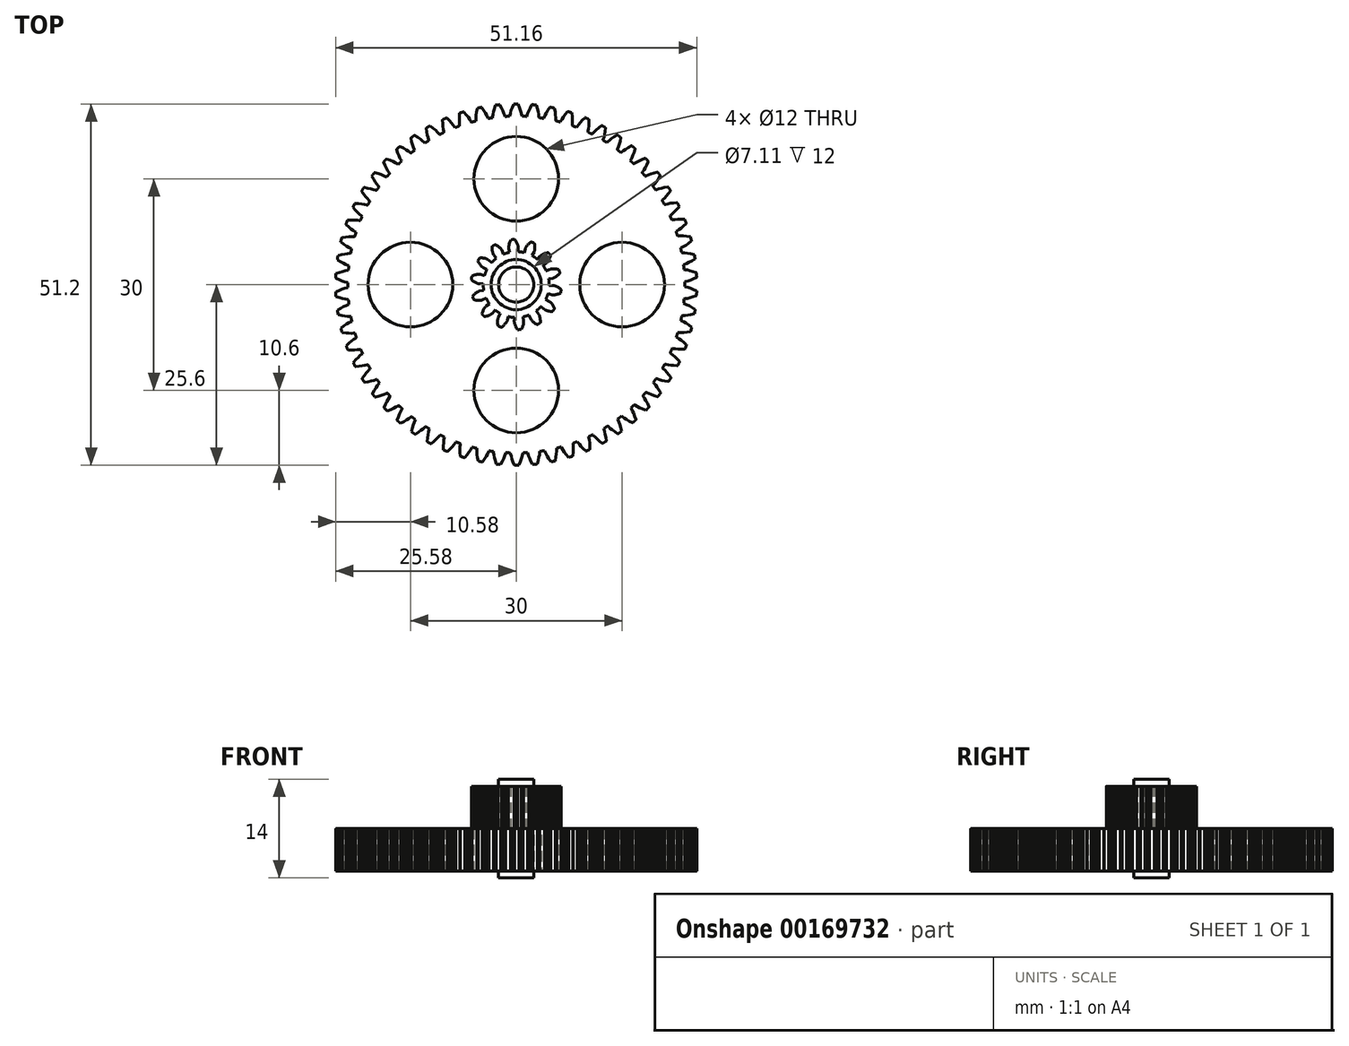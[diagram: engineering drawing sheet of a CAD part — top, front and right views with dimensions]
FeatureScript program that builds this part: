
annotation { "Feature Type Name" : "Feature", "Feature Type Description" : "" }
export const myFeature = defineFeature(function(context is Context, id is Id, definition is map)
    precondition{}
    {
        {
            var Q0;
            Q0=qCreatedBy(makeId("Top.planeOp"),FACE);
            var sketch = newSketch(context, id + "F0", { "sketchPlane" : qUnion([Q0])});
            skLineSegment(sketch, "E0", {"start": v(3, 3.59) * mm, "end": v(3.37, 4.04) * mm});
            skLineSegment(sketch, "E1", {"start": v(3.37, 4.04) * mm, "end": v(3.38, 4.04) * mm});
            skLineSegment(sketch, "E2", {"start": v(3.38, 4.04) * mm, "end": v(3.4, 4.06) * mm});
            skLineSegment(sketch, "E3", {"start": v(3.4, 4.06) * mm, "end": v(3.41, 4.08) * mm});
            skLineSegment(sketch, "E4", {"start": v(3.41, 4.08) * mm, "end": v(3.45, 4.11) * mm});
            skLineSegment(sketch, "E5", {"start": v(3.45, 4.11) * mm, "end": v(3.5, 4.15) * mm});
            skLineSegment(sketch, "E6", {"start": v(3.5, 4.15) * mm, "end": v(3.56, 4.19) * mm});
            skLineSegment(sketch, "E7", {"start": v(3.56, 4.19) * mm, "end": v(3.63, 4.23) * mm});
            skLineSegment(sketch, "E8", {"start": v(3.63, 4.23) * mm, "end": v(3.72, 4.28) * mm});
            skLineSegment(sketch, "E9", {"start": v(3.72, 4.28) * mm, "end": v(3.82, 4.33) * mm});
            skLineSegment(sketch, "E10", {"start": v(3.82, 4.33) * mm, "end": v(3.93, 4.38) * mm});
            skLineSegment(sketch, "E11", {"start": v(3.93, 4.38) * mm, "end": v(4.06, 4.42) * mm});
            skLineSegment(sketch, "E12", {"start": v(4.06, 4.42) * mm, "end": v(4.2, 4.47) * mm});
            skLineSegment(sketch, "E13", {"start": v(4.2, 4.47) * mm, "end": v(4.37, 4.5) * mm});
            skLineSegment(sketch, "E14", {"start": v(4.37, 4.5) * mm, "end": v(4.51, 4.54) * mm});
            skArc(sketch, "E15", {"start": v(4.51, 4.54) * mm, "mid": v(4.7, 4.35) * mm, "end": v(4.86, 4.16) * mm});
            skLineSegment(sketch, "E16", {"start": v(4.86, 4.16) * mm, "end": v(4.82, 4.02) * mm});
            skLineSegment(sketch, "E17", {"start": v(4.82, 4.02) * mm, "end": v(4.77, 3.86) * mm});
            skLineSegment(sketch, "E18", {"start": v(4.77, 3.86) * mm, "end": v(4.72, 3.72) * mm});
            skLineSegment(sketch, "E19", {"start": v(4.72, 3.72) * mm, "end": v(4.66, 3.6) * mm});
            skLineSegment(sketch, "E20", {"start": v(4.66, 3.6) * mm, "end": v(4.6, 3.48) * mm});
            skLineSegment(sketch, "E21", {"start": v(4.6, 3.48) * mm, "end": v(4.55, 3.39) * mm});
            skLineSegment(sketch, "E22", {"start": v(4.55, 3.39) * mm, "end": v(4.5, 3.3) * mm});
            skLineSegment(sketch, "E23", {"start": v(4.5, 3.3) * mm, "end": v(4.44, 3.23) * mm});
            skLineSegment(sketch, "E24", {"start": v(4.44, 3.23) * mm, "end": v(4.4, 3.18) * mm});
            skLineSegment(sketch, "E25", {"start": v(4.4, 3.18) * mm, "end": v(4.36, 3.13) * mm});
            skLineSegment(sketch, "E26", {"start": v(4.36, 3.13) * mm, "end": v(4.32, 3.1) * mm});
            skLineSegment(sketch, "E27", {"start": v(4.32, 3.1) * mm, "end": v(4.3, 3.08) * mm});
            skLineSegment(sketch, "E28", {"start": v(4.3, 3.08) * mm, "end": v(4.29, 3.06) * mm});
            skLineSegment(sketch, "E29", {"start": v(4.29, 3.06) * mm, "end": v(4.28, 3.06) * mm});
            skLineSegment(sketch, "E30", {"start": v(4.28, 3.06) * mm, "end": v(3.8, 2.72) * mm});
            skArc(sketch, "E31", {"start": v(3.8, 2.72) * mm, "mid": v(4.05, 2.34) * mm, "end": v(4.26, 1.93) * mm});
            skLineSegment(sketch, "E32", {"start": v(4.26, 1.93) * mm, "end": v(4.8, 2.18) * mm});
            skLineSegment(sketch, "E33", {"start": v(4.8, 2.18) * mm, "end": v(4.8, 2.18) * mm});
            skLineSegment(sketch, "E34", {"start": v(4.8, 2.18) * mm, "end": v(4.82, 2.19) * mm});
            skLineSegment(sketch, "E35", {"start": v(4.82, 2.19) * mm, "end": v(4.85, 2.2) * mm});
            skLineSegment(sketch, "E36", {"start": v(4.85, 2.2) * mm, "end": v(4.9, 2.2) * mm});
            skLineSegment(sketch, "E37", {"start": v(4.9, 2.2) * mm, "end": v(4.95, 2.22) * mm});
            skLineSegment(sketch, "E38", {"start": v(4.95, 2.22) * mm, "end": v(5.02, 2.23) * mm});
            skLineSegment(sketch, "E39", {"start": v(5.02, 2.23) * mm, "end": v(5.1, 2.24) * mm});
            skLineSegment(sketch, "E40", {"start": v(5.1, 2.24) * mm, "end": v(5.2, 2.24) * mm});
            skLineSegment(sketch, "E41", {"start": v(5.2, 2.24) * mm, "end": v(5.32, 2.24) * mm});
            skLineSegment(sketch, "E42", {"start": v(5.32, 2.24) * mm, "end": v(5.44, 2.24) * mm});
            skLineSegment(sketch, "E43", {"start": v(5.44, 2.24) * mm, "end": v(5.58, 2.22) * mm});
            skLineSegment(sketch, "E44", {"start": v(5.58, 2.22) * mm, "end": v(5.73, 2.2) * mm});
            skLineSegment(sketch, "E45", {"start": v(5.73, 2.2) * mm, "end": v(5.89, 2.17) * mm});
            skLineSegment(sketch, "E46", {"start": v(5.89, 2.17) * mm, "end": v(6.03, 2.13) * mm});
            skArc(sketch, "E47", {"start": v(6.03, 2.13) * mm, "mid": v(6.12, 1.89) * mm, "end": v(6.19, 1.64) * mm});
            skLineSegment(sketch, "E48", {"start": v(6.19, 1.64) * mm, "end": v(6.09, 1.53) * mm});
            skLineSegment(sketch, "E49", {"start": v(6.09, 1.53) * mm, "end": v(5.97, 1.4) * mm});
            skLineSegment(sketch, "E50", {"start": v(5.97, 1.4) * mm, "end": v(5.86, 1.3) * mm});
            skLineSegment(sketch, "E51", {"start": v(5.86, 1.3) * mm, "end": v(5.76, 1.22) * mm});
            skLineSegment(sketch, "E52", {"start": v(5.76, 1.22) * mm, "end": v(5.66, 1.14) * mm});
            skLineSegment(sketch, "E53", {"start": v(5.66, 1.14) * mm, "end": v(5.56, 1.08) * mm});
            skLineSegment(sketch, "E54", {"start": v(5.56, 1.08) * mm, "end": v(5.48, 1.03) * mm});
            skLineSegment(sketch, "E55", {"start": v(5.48, 1.03) * mm, "end": v(5.4, 0.99) * mm});
            skLineSegment(sketch, "E56", {"start": v(5.4, 0.99) * mm, "end": v(5.34, 0.96) * mm});
            skLineSegment(sketch, "E57", {"start": v(5.34, 0.96) * mm, "end": v(5.28, 0.93) * mm});
            skLineSegment(sketch, "E58", {"start": v(5.28, 0.93) * mm, "end": v(5.24, 0.92) * mm});
            skLineSegment(sketch, "E59", {"start": v(5.24, 0.92) * mm, "end": v(5.21, 0.9) * mm});
            skLineSegment(sketch, "E60", {"start": v(5.21, 0.9) * mm, "end": v(5.2, 0.9) * mm});
            skLineSegment(sketch, "E61", {"start": v(5.2, 0.9) * mm, "end": v(5.18, 0.9) * mm});
            skLineSegment(sketch, "E62", {"start": v(5.18, 0.9) * mm, "end": v(4.6, 0.8) * mm});
            skArc(sketch, "E63", {"start": v(4.6, 0.8) * mm, "mid": v(4.66, 0.35) * mm, "end": v(4.67, -0.1) * mm});
            skLineSegment(sketch, "E64", {"start": v(4.67, -0.1) * mm, "end": v(5.26, -0.12) * mm});
            skLineSegment(sketch, "E65", {"start": v(5.26, -0.12) * mm, "end": v(5.27, -0.12) * mm});
            skLineSegment(sketch, "E66", {"start": v(5.27, -0.12) * mm, "end": v(5.29, -0.12) * mm});
            skLineSegment(sketch, "E67", {"start": v(5.29, -0.12) * mm, "end": v(5.32, -0.13) * mm});
            skLineSegment(sketch, "E68", {"start": v(5.32, -0.13) * mm, "end": v(5.36, -0.13) * mm});
            skLineSegment(sketch, "E69", {"start": v(5.36, -0.13) * mm, "end": v(5.42, -0.15) * mm});
            skLineSegment(sketch, "E70", {"start": v(5.42, -0.15) * mm, "end": v(5.5, -0.17) * mm});
            skLineSegment(sketch, "E71", {"start": v(5.5, -0.17) * mm, "end": v(5.57, -0.2) * mm});
            skLineSegment(sketch, "E72", {"start": v(5.57, -0.2) * mm, "end": v(5.66, -0.24) * mm});
            skLineSegment(sketch, "E73", {"start": v(5.66, -0.24) * mm, "end": v(5.76, -0.29) * mm});
            skLineSegment(sketch, "E74", {"start": v(5.76, -0.29) * mm, "end": v(5.87, -0.35) * mm});
            skLineSegment(sketch, "E75", {"start": v(5.87, -0.35) * mm, "end": v(6, -0.42) * mm});
            skLineSegment(sketch, "E76", {"start": v(6, -0.42) * mm, "end": v(6.12, -0.5) * mm});
            skLineSegment(sketch, "E77", {"start": v(6.12, -0.5) * mm, "end": v(6.25, -0.6) * mm});
            skLineSegment(sketch, "E78", {"start": v(6.25, -0.6) * mm, "end": v(6.36, -0.7) * mm});
            skArc(sketch, "E79", {"start": v(6.36, -0.7) * mm, "mid": v(6.33, -0.95) * mm, "end": v(6.28, -1.2) * mm});
            skLineSegment(sketch, "E80", {"start": v(6.28, -1.2) * mm, "end": v(6.15, -1.27) * mm});
            skLineSegment(sketch, "E81", {"start": v(6.15, -1.27) * mm, "end": v(6, -1.32) * mm});
            skLineSegment(sketch, "E82", {"start": v(6, -1.32) * mm, "end": v(5.85, -1.37) * mm});
            skLineSegment(sketch, "E83", {"start": v(5.85, -1.37) * mm, "end": v(5.71, -1.4) * mm});
            skLineSegment(sketch, "E84", {"start": v(5.71, -1.4) * mm, "end": v(5.6, -1.43) * mm});
            skLineSegment(sketch, "E85", {"start": v(5.6, -1.43) * mm, "end": v(5.48, -1.44) * mm});
            skLineSegment(sketch, "E86", {"start": v(5.48, -1.44) * mm, "end": v(5.38, -1.45) * mm});
            skLineSegment(sketch, "E87", {"start": v(5.38, -1.45) * mm, "end": v(5.3, -1.46) * mm});
            skLineSegment(sketch, "E88", {"start": v(5.3, -1.46) * mm, "end": v(5.23, -1.46) * mm});
            skLineSegment(sketch, "E89", {"start": v(5.23, -1.46) * mm, "end": v(5.17, -1.45) * mm});
            skLineSegment(sketch, "E90", {"start": v(5.17, -1.45) * mm, "end": v(5.12, -1.45) * mm});
            skLineSegment(sketch, "E91", {"start": v(5.12, -1.45) * mm, "end": v(5.09, -1.44) * mm});
            skLineSegment(sketch, "E92", {"start": v(5.09, -1.44) * mm, "end": v(5.07, -1.44) * mm});
            skLineSegment(sketch, "E93", {"start": v(5.07, -1.44) * mm, "end": v(5.06, -1.44) * mm});
            skLineSegment(sketch, "E94", {"start": v(5.06, -1.44) * mm, "end": v(4.5, -1.28) * mm});
            skArc(sketch, "E95", {"start": v(4.5, -1.28) * mm, "mid": v(4.35, -1.7) * mm, "end": v(4.16, -2.12) * mm});
            skLineSegment(sketch, "E96", {"start": v(4.16, -2.12) * mm, "end": v(4.69, -2.39) * mm});
            skLineSegment(sketch, "E97", {"start": v(4.69, -2.39) * mm, "end": v(4.7, -2.4) * mm});
            skLineSegment(sketch, "E98", {"start": v(4.7, -2.4) * mm, "end": v(4.71, -2.4) * mm});
            skLineSegment(sketch, "E99", {"start": v(4.71, -2.4) * mm, "end": v(4.74, -2.42) * mm});
            skLineSegment(sketch, "E100", {"start": v(4.74, -2.42) * mm, "end": v(4.78, -2.45) * mm});
            skLineSegment(sketch, "E101", {"start": v(4.78, -2.45) * mm, "end": v(4.82, -2.49) * mm});
            skLineSegment(sketch, "E102", {"start": v(4.82, -2.49) * mm, "end": v(4.87, -2.54) * mm});
            skLineSegment(sketch, "E103", {"start": v(4.87, -2.54) * mm, "end": v(4.93, -2.6) * mm});
            skLineSegment(sketch, "E104", {"start": v(4.93, -2.6) * mm, "end": v(5, -2.67) * mm});
            skLineSegment(sketch, "E105", {"start": v(5, -2.67) * mm, "end": v(5.07, -2.76) * mm});
            skLineSegment(sketch, "E106", {"start": v(5.07, -2.76) * mm, "end": v(5.14, -2.86) * mm});
            skLineSegment(sketch, "E107", {"start": v(5.14, -2.86) * mm, "end": v(5.22, -2.98) * mm});
            skLineSegment(sketch, "E108", {"start": v(5.22, -2.98) * mm, "end": v(5.3, -3.1) * mm});
            skLineSegment(sketch, "E109", {"start": v(5.3, -3.1) * mm, "end": v(5.37, -3.25) * mm});
            skLineSegment(sketch, "E110", {"start": v(5.37, -3.25) * mm, "end": v(5.43, -3.39) * mm});
            skArc(sketch, "E111", {"start": v(5.43, -3.39) * mm, "mid": v(5.29, -3.6) * mm, "end": v(5.14, -3.82) * mm});
            skLineSegment(sketch, "E112", {"start": v(5.14, -3.82) * mm, "end": v(4.99, -3.8) * mm});
            skLineSegment(sketch, "E113", {"start": v(4.99, -3.8) * mm, "end": v(4.83, -3.8) * mm});
            skLineSegment(sketch, "E114", {"start": v(4.83, -3.8) * mm, "end": v(4.68, -3.77) * mm});
            skLineSegment(sketch, "E115", {"start": v(4.68, -3.77) * mm, "end": v(4.54, -3.74) * mm});
            skLineSegment(sketch, "E116", {"start": v(4.54, -3.74) * mm, "end": v(4.42, -3.71) * mm});
            skLineSegment(sketch, "E117", {"start": v(4.42, -3.71) * mm, "end": v(4.31, -3.68) * mm});
            skLineSegment(sketch, "E118", {"start": v(4.31, -3.68) * mm, "end": v(4.22, -3.64) * mm});
            skLineSegment(sketch, "E119", {"start": v(4.22, -3.64) * mm, "end": v(4.14, -3.61) * mm});
            skLineSegment(sketch, "E120", {"start": v(4.14, -3.61) * mm, "end": v(4.08, -3.58) * mm});
            skLineSegment(sketch, "E121", {"start": v(4.08, -3.58) * mm, "end": v(4.02, -3.55) * mm});
            skLineSegment(sketch, "E122", {"start": v(4.02, -3.55) * mm, "end": v(3.98, -3.53) * mm});
            skLineSegment(sketch, "E123", {"start": v(3.98, -3.53) * mm, "end": v(3.96, -3.5) * mm});
            skLineSegment(sketch, "E124", {"start": v(3.96, -3.5) * mm, "end": v(3.94, -3.5) * mm});
            skLineSegment(sketch, "E125", {"start": v(3.94, -3.5) * mm, "end": v(3.94, -3.5) * mm});
            skLineSegment(sketch, "E126", {"start": v(3.94, -3.5) * mm, "end": v(3.5, -3.1) * mm});
            skArc(sketch, "E127", {"start": v(3.5, -3.1) * mm, "mid": v(3.18, -3.43) * mm, "end": v(2.83, -3.72) * mm});
            skLineSegment(sketch, "E128", {"start": v(2.83, -3.72) * mm, "end": v(3.19, -4.19) * mm});
            skLineSegment(sketch, "E129", {"start": v(3.19, -4.19) * mm, "end": v(3.2, -4.2) * mm});
            skLineSegment(sketch, "E130", {"start": v(3.2, -4.2) * mm, "end": v(3.2, -4.2) * mm});
            skLineSegment(sketch, "E131", {"start": v(3.2, -4.2) * mm, "end": v(3.22, -4.24) * mm});
            skLineSegment(sketch, "E132", {"start": v(3.22, -4.24) * mm, "end": v(3.24, -4.28) * mm});
            skLineSegment(sketch, "E133", {"start": v(3.24, -4.28) * mm, "end": v(3.26, -4.33) * mm});
            skLineSegment(sketch, "E134", {"start": v(3.26, -4.33) * mm, "end": v(3.3, -4.4) * mm});
            skLineSegment(sketch, "E135", {"start": v(3.3, -4.4) * mm, "end": v(3.32, -4.48) * mm});
            skLineSegment(sketch, "E136", {"start": v(3.32, -4.48) * mm, "end": v(3.35, -4.58) * mm});
            skLineSegment(sketch, "E137", {"start": v(3.35, -4.58) * mm, "end": v(3.37, -4.68) * mm});
            skLineSegment(sketch, "E138", {"start": v(3.37, -4.68) * mm, "end": v(3.4, -4.8) * mm});
            skLineSegment(sketch, "E139", {"start": v(3.4, -4.8) * mm, "end": v(3.4, -4.94) * mm});
            skLineSegment(sketch, "E140", {"start": v(3.4, -4.94) * mm, "end": v(3.42, -5.1) * mm});
            skLineSegment(sketch, "E141", {"start": v(3.42, -5.1) * mm, "end": v(3.42, -5.26) * mm});
            skLineSegment(sketch, "E142", {"start": v(3.42, -5.26) * mm, "end": v(3.42, -5.4) * mm});
            skArc(sketch, "E143", {"start": v(3.42, -5.4) * mm, "mid": v(3.2, -5.54) * mm, "end": v(2.97, -5.67) * mm});
            skLineSegment(sketch, "E144", {"start": v(2.97, -5.67) * mm, "end": v(2.84, -5.6) * mm});
            skLineSegment(sketch, "E145", {"start": v(2.84, -5.6) * mm, "end": v(2.7, -5.5) * mm});
            skLineSegment(sketch, "E146", {"start": v(2.7, -5.5) * mm, "end": v(2.58, -5.42) * mm});
            skLineSegment(sketch, "E147", {"start": v(2.58, -5.42) * mm, "end": v(2.47, -5.34) * mm});
            skLineSegment(sketch, "E148", {"start": v(2.47, -5.34) * mm, "end": v(2.37, -5.26) * mm});
            skLineSegment(sketch, "E149", {"start": v(2.37, -5.26) * mm, "end": v(2.29, -5.18) * mm});
            skLineSegment(sketch, "E150", {"start": v(2.29, -5.18) * mm, "end": v(2.22, -5.11) * mm});
            skLineSegment(sketch, "E151", {"start": v(2.22, -5.11) * mm, "end": v(2.16, -5.05) * mm});
            skLineSegment(sketch, "E152", {"start": v(2.16, -5.05) * mm, "end": v(2.12, -5) * mm});
            skLineSegment(sketch, "E153", {"start": v(2.12, -5) * mm, "end": v(2.08, -4.94) * mm});
            skLineSegment(sketch, "E154", {"start": v(2.08, -4.94) * mm, "end": v(2.06, -4.9) * mm});
            skLineSegment(sketch, "E155", {"start": v(2.06, -4.9) * mm, "end": v(2.04, -4.88) * mm});
            skLineSegment(sketch, "E156", {"start": v(2.04, -4.88) * mm, "end": v(2.03, -4.86) * mm});
            skLineSegment(sketch, "E157", {"start": v(2.03, -4.86) * mm, "end": v(2.03, -4.85) * mm});
            skLineSegment(sketch, "E158", {"start": v(2.03, -4.85) * mm, "end": v(1.8, -4.31) * mm});
            skArc(sketch, "E159", {"start": v(1.8, -4.31) * mm, "mid": v(1.38, -4.47) * mm, "end": v(0.94, -4.58) * mm});
            skLineSegment(sketch, "E160", {"start": v(0.94, -4.58) * mm, "end": v(1.06, -5.16) * mm});
            skLineSegment(sketch, "E161", {"start": v(1.06, -5.16) * mm, "end": v(1.06, -5.16) * mm});
            skLineSegment(sketch, "E162", {"start": v(1.06, -5.16) * mm, "end": v(1.06, -5.18) * mm});
            skLineSegment(sketch, "E163", {"start": v(1.06, -5.18) * mm, "end": v(1.06, -5.21) * mm});
            skLineSegment(sketch, "E164", {"start": v(1.06, -5.21) * mm, "end": v(1.06, -5.26) * mm});
            skLineSegment(sketch, "E165", {"start": v(1.06, -5.26) * mm, "end": v(1.06, -5.32) * mm});
            skLineSegment(sketch, "E166", {"start": v(1.06, -5.32) * mm, "end": v(1.06, -5.4) * mm});
            skLineSegment(sketch, "E167", {"start": v(1.06, -5.4) * mm, "end": v(1.05, -5.48) * mm});
            skLineSegment(sketch, "E168", {"start": v(1.05, -5.48) * mm, "end": v(1.03, -5.57) * mm});
            skLineSegment(sketch, "E169", {"start": v(1.03, -5.57) * mm, "end": v(1, -5.68) * mm});
            skLineSegment(sketch, "E170", {"start": v(1, -5.68) * mm, "end": v(0.97, -5.8) * mm});
            skLineSegment(sketch, "E171", {"start": v(0.97, -5.8) * mm, "end": v(0.93, -5.93) * mm});
            skLineSegment(sketch, "E172", {"start": v(0.93, -5.93) * mm, "end": v(0.87, -6.07) * mm});
            skLineSegment(sketch, "E173", {"start": v(0.87, -6.07) * mm, "end": v(0.8, -6.22) * mm});
            skLineSegment(sketch, "E174", {"start": v(0.8, -6.22) * mm, "end": v(0.74, -6.36) * mm});
            skArc(sketch, "E175", {"start": v(0.74, -6.36) * mm, "mid": v(0.48, -6.38) * mm, "end": v(0.22, -6.4) * mm});
            skLineSegment(sketch, "E176", {"start": v(0.22, -6.4) * mm, "end": v(0.13, -6.27) * mm});
            skLineSegment(sketch, "E177", {"start": v(0.13, -6.27) * mm, "end": v(0.04, -6.14) * mm});
            skLineSegment(sketch, "E178", {"start": v(0.04, -6.14) * mm, "end": v(-0.03, -6) * mm});
            skLineSegment(sketch, "E179", {"start": v(-0.03, -6) * mm, "end": v(-0.1, -5.88) * mm});
            skLineSegment(sketch, "E180", {"start": v(-0.1, -5.88) * mm, "end": v(-0.15, -5.77) * mm});
            skLineSegment(sketch, "E181", {"start": v(-0.15, -5.77) * mm, "end": v(-0.19, -5.66) * mm});
            skLineSegment(sketch, "E182", {"start": v(-0.19, -5.66) * mm, "end": v(-0.22, -5.57) * mm});
            skLineSegment(sketch, "E183", {"start": v(-0.22, -5.57) * mm, "end": v(-0.24, -5.49) * mm});
            skLineSegment(sketch, "E184", {"start": v(-0.24, -5.49) * mm, "end": v(-0.26, -5.42) * mm});
            skLineSegment(sketch, "E185", {"start": v(-0.26, -5.42) * mm, "end": v(-0.27, -5.36) * mm});
            skLineSegment(sketch, "E186", {"start": v(-0.27, -5.36) * mm, "end": v(-0.27, -5.31) * mm});
            skLineSegment(sketch, "E187", {"start": v(-0.27, -5.31) * mm, "end": v(-0.28, -5.28) * mm});
            skLineSegment(sketch, "E188", {"start": v(-0.28, -5.28) * mm, "end": v(-0.28, -5.26) * mm});
            skLineSegment(sketch, "E189", {"start": v(-0.28, -5.26) * mm, "end": v(-0.28, -5.26) * mm});
            skLineSegment(sketch, "E190", {"start": v(-0.28, -5.26) * mm, "end": v(-0.24, -4.67) * mm});
            skArc(sketch, "E191", {"start": v(-0.24, -4.67) * mm, "mid": v(-0.7, -4.62) * mm, "end": v(-1.14, -4.53) * mm});
            skLineSegment(sketch, "E192", {"start": v(-1.14, -4.53) * mm, "end": v(-1.29, -5.1) * mm});
            skLineSegment(sketch, "E193", {"start": v(-1.29, -5.1) * mm, "end": v(-1.29, -5.1) * mm});
            skLineSegment(sketch, "E194", {"start": v(-1.29, -5.1) * mm, "end": v(-1.3, -5.13) * mm});
            skLineSegment(sketch, "E195", {"start": v(-1.3, -5.13) * mm, "end": v(-1.3, -5.16) * mm});
            skLineSegment(sketch, "E196", {"start": v(-1.3, -5.16) * mm, "end": v(-1.32, -5.2) * mm});
            skLineSegment(sketch, "E197", {"start": v(-1.32, -5.2) * mm, "end": v(-1.35, -5.25) * mm});
            skLineSegment(sketch, "E198", {"start": v(-1.35, -5.25) * mm, "end": v(-1.39, -5.32) * mm});
            skLineSegment(sketch, "E199", {"start": v(-1.39, -5.32) * mm, "end": v(-1.43, -5.39) * mm});
            skLineSegment(sketch, "E200", {"start": v(-1.43, -5.39) * mm, "end": v(-1.5, -5.47) * mm});
            skLineSegment(sketch, "E201", {"start": v(-1.5, -5.47) * mm, "end": v(-1.56, -5.56) * mm});
            skLineSegment(sketch, "E202", {"start": v(-1.56, -5.56) * mm, "end": v(-1.64, -5.65) * mm});
            skLineSegment(sketch, "E203", {"start": v(-1.64, -5.65) * mm, "end": v(-1.74, -5.75) * mm});
            skLineSegment(sketch, "E204", {"start": v(-1.74, -5.75) * mm, "end": v(-1.85, -5.85) * mm});
            skLineSegment(sketch, "E205", {"start": v(-1.85, -5.85) * mm, "end": v(-1.98, -5.96) * mm});
            skLineSegment(sketch, "E206", {"start": v(-1.98, -5.96) * mm, "end": v(-2.1, -6.05) * mm});
            skArc(sketch, "E207", {"start": v(-2.1, -6.05) * mm, "mid": v(-2.34, -5.96) * mm, "end": v(-2.58, -5.86) * mm});
            skLineSegment(sketch, "E208", {"start": v(-2.58, -5.86) * mm, "end": v(-2.6, -5.71) * mm});
            skLineSegment(sketch, "E209", {"start": v(-2.6, -5.71) * mm, "end": v(-2.62, -5.55) * mm});
            skLineSegment(sketch, "E210", {"start": v(-2.62, -5.55) * mm, "end": v(-2.63, -5.4) * mm});
            skLineSegment(sketch, "E211", {"start": v(-2.63, -5.4) * mm, "end": v(-2.64, -5.26) * mm});
            skLineSegment(sketch, "E212", {"start": v(-2.64, -5.26) * mm, "end": v(-2.63, -5.13) * mm});
            skLineSegment(sketch, "E213", {"start": v(-2.63, -5.13) * mm, "end": v(-2.63, -5.02) * mm});
            skLineSegment(sketch, "E214", {"start": v(-2.63, -5.02) * mm, "end": v(-2.61, -4.92) * mm});
            skLineSegment(sketch, "E215", {"start": v(-2.61, -4.92) * mm, "end": v(-2.6, -4.84) * mm});
            skLineSegment(sketch, "E216", {"start": v(-2.6, -4.84) * mm, "end": v(-2.58, -4.77) * mm});
            skLineSegment(sketch, "E217", {"start": v(-2.58, -4.77) * mm, "end": v(-2.57, -4.71) * mm});
            skLineSegment(sketch, "E218", {"start": v(-2.57, -4.71) * mm, "end": v(-2.55, -4.67) * mm});
            skLineSegment(sketch, "E219", {"start": v(-2.55, -4.67) * mm, "end": v(-2.54, -4.64) * mm});
            skLineSegment(sketch, "E220", {"start": v(-2.54, -4.64) * mm, "end": v(-2.53, -4.62) * mm});
            skLineSegment(sketch, "E221", {"start": v(-2.53, -4.62) * mm, "end": v(-2.53, -4.62) * mm});
            skLineSegment(sketch, "E222", {"start": v(-2.53, -4.62) * mm, "end": v(-2.25, -4.1) * mm});
            skArc(sketch, "E223", {"start": v(-2.25, -4.1) * mm, "mid": v(-2.63, -3.86) * mm, "end": v(-3, -3.59) * mm});
            skLineSegment(sketch, "E224", {"start": v(-3, -3.59) * mm, "end": v(-3.37, -4.04) * mm});
            skLineSegment(sketch, "E225", {"start": v(-3.37, -4.04) * mm, "end": v(-3.38, -4.04) * mm});
            skLineSegment(sketch, "E226", {"start": v(-3.38, -4.04) * mm, "end": v(-3.4, -4.06) * mm});
            skLineSegment(sketch, "E227", {"start": v(-3.4, -4.06) * mm, "end": v(-3.41, -4.08) * mm});
            skLineSegment(sketch, "E228", {"start": v(-3.41, -4.08) * mm, "end": v(-3.45, -4.11) * mm});
            skLineSegment(sketch, "E229", {"start": v(-3.45, -4.11) * mm, "end": v(-3.5, -4.15) * mm});
            skLineSegment(sketch, "E230", {"start": v(-3.5, -4.15) * mm, "end": v(-3.56, -4.19) * mm});
            skLineSegment(sketch, "E231", {"start": v(-3.56, -4.19) * mm, "end": v(-3.63, -4.23) * mm});
            skLineSegment(sketch, "E232", {"start": v(-3.63, -4.23) * mm, "end": v(-3.72, -4.28) * mm});
            skLineSegment(sketch, "E233", {"start": v(-3.72, -4.28) * mm, "end": v(-3.82, -4.33) * mm});
            skLineSegment(sketch, "E234", {"start": v(-3.82, -4.33) * mm, "end": v(-3.93, -4.38) * mm});
            skLineSegment(sketch, "E235", {"start": v(-3.93, -4.38) * mm, "end": v(-4.06, -4.42) * mm});
            skLineSegment(sketch, "E236", {"start": v(-4.06, -4.42) * mm, "end": v(-4.2, -4.47) * mm});
            skLineSegment(sketch, "E237", {"start": v(-4.2, -4.47) * mm, "end": v(-4.37, -4.5) * mm});
            skLineSegment(sketch, "E238", {"start": v(-4.37, -4.5) * mm, "end": v(-4.51, -4.54) * mm});
            skArc(sketch, "E239", {"start": v(-4.51, -4.54) * mm, "mid": v(-4.7, -4.35) * mm, "end": v(-4.86, -4.16) * mm});
            skLineSegment(sketch, "E240", {"start": v(-4.86, -4.16) * mm, "end": v(-4.82, -4.02) * mm});
            skLineSegment(sketch, "E241", {"start": v(-4.82, -4.02) * mm, "end": v(-4.77, -3.86) * mm});
            skLineSegment(sketch, "E242", {"start": v(-4.77, -3.86) * mm, "end": v(-4.72, -3.72) * mm});
            skLineSegment(sketch, "E243", {"start": v(-4.72, -3.72) * mm, "end": v(-4.66, -3.6) * mm});
            skLineSegment(sketch, "E244", {"start": v(-4.66, -3.6) * mm, "end": v(-4.6, -3.48) * mm});
            skLineSegment(sketch, "E245", {"start": v(-4.6, -3.48) * mm, "end": v(-4.55, -3.39) * mm});
            skLineSegment(sketch, "E246", {"start": v(-4.55, -3.39) * mm, "end": v(-4.5, -3.3) * mm});
            skLineSegment(sketch, "E247", {"start": v(-4.5, -3.3) * mm, "end": v(-4.44, -3.23) * mm});
            skLineSegment(sketch, "E248", {"start": v(-4.44, -3.23) * mm, "end": v(-4.4, -3.18) * mm});
            skLineSegment(sketch, "E249", {"start": v(-4.4, -3.18) * mm, "end": v(-4.36, -3.13) * mm});
            skLineSegment(sketch, "E250", {"start": v(-4.36, -3.13) * mm, "end": v(-4.32, -3.1) * mm});
            skLineSegment(sketch, "E251", {"start": v(-4.32, -3.1) * mm, "end": v(-4.3, -3.08) * mm});
            skLineSegment(sketch, "E252", {"start": v(-4.3, -3.08) * mm, "end": v(-4.29, -3.06) * mm});
            skLineSegment(sketch, "E253", {"start": v(-4.29, -3.06) * mm, "end": v(-4.28, -3.06) * mm});
            skLineSegment(sketch, "E254", {"start": v(-4.28, -3.06) * mm, "end": v(-3.8, -2.72) * mm});
            skArc(sketch, "E255", {"start": v(-3.8, -2.72) * mm, "mid": v(-4.05, -2.34) * mm, "end": v(-4.26, -1.93) * mm});
            skLineSegment(sketch, "E256", {"start": v(-4.26, -1.93) * mm, "end": v(-4.8, -2.18) * mm});
            skLineSegment(sketch, "E257", {"start": v(-4.8, -2.18) * mm, "end": v(-4.8, -2.18) * mm});
            skLineSegment(sketch, "E258", {"start": v(-4.8, -2.18) * mm, "end": v(-4.82, -2.19) * mm});
            skLineSegment(sketch, "E259", {"start": v(-4.82, -2.19) * mm, "end": v(-4.85, -2.2) * mm});
            skLineSegment(sketch, "E260", {"start": v(-4.85, -2.2) * mm, "end": v(-4.9, -2.2) * mm});
            skLineSegment(sketch, "E261", {"start": v(-4.9, -2.2) * mm, "end": v(-4.95, -2.22) * mm});
            skLineSegment(sketch, "E262", {"start": v(-4.95, -2.22) * mm, "end": v(-5.02, -2.23) * mm});
            skLineSegment(sketch, "E263", {"start": v(-5.02, -2.23) * mm, "end": v(-5.1, -2.24) * mm});
            skLineSegment(sketch, "E264", {"start": v(-5.1, -2.24) * mm, "end": v(-5.2, -2.24) * mm});
            skLineSegment(sketch, "E265", {"start": v(-5.2, -2.24) * mm, "end": v(-5.32, -2.24) * mm});
            skLineSegment(sketch, "E266", {"start": v(-5.32, -2.24) * mm, "end": v(-5.44, -2.24) * mm});
            skLineSegment(sketch, "E267", {"start": v(-5.44, -2.24) * mm, "end": v(-5.58, -2.22) * mm});
            skLineSegment(sketch, "E268", {"start": v(-5.58, -2.22) * mm, "end": v(-5.73, -2.2) * mm});
            skLineSegment(sketch, "E269", {"start": v(-5.73, -2.2) * mm, "end": v(-5.89, -2.17) * mm});
            skLineSegment(sketch, "E270", {"start": v(-5.89, -2.17) * mm, "end": v(-6.03, -2.13) * mm});
            skArc(sketch, "E271", {"start": v(-6.03, -2.13) * mm, "mid": v(-6.12, -1.89) * mm, "end": v(-6.19, -1.64) * mm});
            skLineSegment(sketch, "E272", {"start": v(-6.19, -1.64) * mm, "end": v(-6.09, -1.53) * mm});
            skLineSegment(sketch, "E273", {"start": v(-6.09, -1.53) * mm, "end": v(-5.97, -1.4) * mm});
            skLineSegment(sketch, "E274", {"start": v(-5.97, -1.4) * mm, "end": v(-5.86, -1.3) * mm});
            skLineSegment(sketch, "E275", {"start": v(-5.86, -1.3) * mm, "end": v(-5.76, -1.22) * mm});
            skLineSegment(sketch, "E276", {"start": v(-5.76, -1.22) * mm, "end": v(-5.66, -1.14) * mm});
            skLineSegment(sketch, "E277", {"start": v(-5.66, -1.14) * mm, "end": v(-5.56, -1.08) * mm});
            skLineSegment(sketch, "E278", {"start": v(-5.56, -1.08) * mm, "end": v(-5.48, -1.03) * mm});
            skLineSegment(sketch, "E279", {"start": v(-5.48, -1.03) * mm, "end": v(-5.4, -0.99) * mm});
            skLineSegment(sketch, "E280", {"start": v(-5.4, -0.99) * mm, "end": v(-5.34, -0.96) * mm});
            skLineSegment(sketch, "E281", {"start": v(-5.34, -0.96) * mm, "end": v(-5.28, -0.93) * mm});
            skLineSegment(sketch, "E282", {"start": v(-5.28, -0.93) * mm, "end": v(-5.24, -0.92) * mm});
            skLineSegment(sketch, "E283", {"start": v(-5.24, -0.92) * mm, "end": v(-5.21, -0.9) * mm});
            skLineSegment(sketch, "E284", {"start": v(-5.21, -0.9) * mm, "end": v(-5.2, -0.9) * mm});
            skLineSegment(sketch, "E285", {"start": v(-5.2, -0.9) * mm, "end": v(-5.18, -0.9) * mm});
            skLineSegment(sketch, "E286", {"start": v(-5.18, -0.9) * mm, "end": v(-4.6, -0.8) * mm});
            skArc(sketch, "E287", {"start": v(-4.6, -0.8) * mm, "mid": v(-4.66, -0.35) * mm, "end": v(-4.67, 0.1) * mm});
            skLineSegment(sketch, "E288", {"start": v(-4.67, 0.1) * mm, "end": v(-5.26, 0.12) * mm});
            skLineSegment(sketch, "E289", {"start": v(-5.26, 0.12) * mm, "end": v(-5.27, 0.12) * mm});
            skLineSegment(sketch, "E290", {"start": v(-5.27, 0.12) * mm, "end": v(-5.29, 0.12) * mm});
            skLineSegment(sketch, "E291", {"start": v(-5.29, 0.12) * mm, "end": v(-5.32, 0.13) * mm});
            skLineSegment(sketch, "E292", {"start": v(-5.32, 0.13) * mm, "end": v(-5.36, 0.13) * mm});
            skLineSegment(sketch, "E293", {"start": v(-5.36, 0.13) * mm, "end": v(-5.42, 0.15) * mm});
            skLineSegment(sketch, "E294", {"start": v(-5.42, 0.15) * mm, "end": v(-5.5, 0.17) * mm});
            skLineSegment(sketch, "E295", {"start": v(-5.5, 0.17) * mm, "end": v(-5.57, 0.2) * mm});
            skLineSegment(sketch, "E296", {"start": v(-5.57, 0.2) * mm, "end": v(-5.66, 0.24) * mm});
            skLineSegment(sketch, "E297", {"start": v(-5.66, 0.24) * mm, "end": v(-5.76, 0.29) * mm});
            skLineSegment(sketch, "E298", {"start": v(-5.76, 0.29) * mm, "end": v(-5.87, 0.35) * mm});
            skLineSegment(sketch, "E299", {"start": v(-5.87, 0.35) * mm, "end": v(-6, 0.42) * mm});
            skLineSegment(sketch, "E300", {"start": v(-6, 0.42) * mm, "end": v(-6.12, 0.5) * mm});
            skLineSegment(sketch, "E301", {"start": v(-6.12, 0.5) * mm, "end": v(-6.25, 0.6) * mm});
            skLineSegment(sketch, "E302", {"start": v(-6.25, 0.6) * mm, "end": v(-6.36, 0.7) * mm});
            skArc(sketch, "E303", {"start": v(-6.36, 0.7) * mm, "mid": v(-6.33, 0.95) * mm, "end": v(-6.28, 1.2) * mm});
            skLineSegment(sketch, "E304", {"start": v(-6.28, 1.2) * mm, "end": v(-6.15, 1.27) * mm});
            skLineSegment(sketch, "E305", {"start": v(-6.15, 1.27) * mm, "end": v(-6, 1.32) * mm});
            skLineSegment(sketch, "E306", {"start": v(-6, 1.32) * mm, "end": v(-5.85, 1.37) * mm});
            skLineSegment(sketch, "E307", {"start": v(-5.85, 1.37) * mm, "end": v(-5.71, 1.4) * mm});
            skLineSegment(sketch, "E308", {"start": v(-5.71, 1.4) * mm, "end": v(-5.6, 1.43) * mm});
            skLineSegment(sketch, "E309", {"start": v(-5.6, 1.43) * mm, "end": v(-5.48, 1.44) * mm});
            skLineSegment(sketch, "E310", {"start": v(-5.48, 1.44) * mm, "end": v(-5.38, 1.45) * mm});
            skLineSegment(sketch, "E311", {"start": v(-5.38, 1.45) * mm, "end": v(-5.3, 1.46) * mm});
            skLineSegment(sketch, "E312", {"start": v(-5.3, 1.46) * mm, "end": v(-5.23, 1.46) * mm});
            skLineSegment(sketch, "E313", {"start": v(-5.23, 1.46) * mm, "end": v(-5.17, 1.45) * mm});
            skLineSegment(sketch, "E314", {"start": v(-5.17, 1.45) * mm, "end": v(-5.12, 1.45) * mm});
            skLineSegment(sketch, "E315", {"start": v(-5.12, 1.45) * mm, "end": v(-5.09, 1.44) * mm});
            skLineSegment(sketch, "E316", {"start": v(-5.09, 1.44) * mm, "end": v(-5.07, 1.44) * mm});
            skLineSegment(sketch, "E317", {"start": v(-5.07, 1.44) * mm, "end": v(-5.06, 1.44) * mm});
            skLineSegment(sketch, "E318", {"start": v(-5.06, 1.44) * mm, "end": v(-4.5, 1.28) * mm});
            skArc(sketch, "E319", {"start": v(-4.5, 1.28) * mm, "mid": v(-4.35, 1.7) * mm, "end": v(-4.16, 2.12) * mm});
            skLineSegment(sketch, "E320", {"start": v(-4.16, 2.12) * mm, "end": v(-4.69, 2.39) * mm});
            skLineSegment(sketch, "E321", {"start": v(-4.69, 2.39) * mm, "end": v(-4.7, 2.4) * mm});
            skLineSegment(sketch, "E322", {"start": v(-4.7, 2.4) * mm, "end": v(-4.71, 2.4) * mm});
            skLineSegment(sketch, "E323", {"start": v(-4.71, 2.4) * mm, "end": v(-4.74, 2.42) * mm});
            skLineSegment(sketch, "E324", {"start": v(-4.74, 2.42) * mm, "end": v(-4.78, 2.45) * mm});
            skLineSegment(sketch, "E325", {"start": v(-4.78, 2.45) * mm, "end": v(-4.82, 2.49) * mm});
            skLineSegment(sketch, "E326", {"start": v(-4.82, 2.49) * mm, "end": v(-4.87, 2.54) * mm});
            skLineSegment(sketch, "E327", {"start": v(-4.87, 2.54) * mm, "end": v(-4.93, 2.6) * mm});
            skLineSegment(sketch, "E328", {"start": v(-4.93, 2.6) * mm, "end": v(-5, 2.67) * mm});
            skLineSegment(sketch, "E329", {"start": v(-5, 2.67) * mm, "end": v(-5.07, 2.76) * mm});
            skLineSegment(sketch, "E330", {"start": v(-5.07, 2.76) * mm, "end": v(-5.14, 2.86) * mm});
            skLineSegment(sketch, "E331", {"start": v(-5.14, 2.86) * mm, "end": v(-5.22, 2.98) * mm});
            skLineSegment(sketch, "E332", {"start": v(-5.22, 2.98) * mm, "end": v(-5.3, 3.1) * mm});
            skLineSegment(sketch, "E333", {"start": v(-5.3, 3.1) * mm, "end": v(-5.37, 3.25) * mm});
            skLineSegment(sketch, "E334", {"start": v(-5.37, 3.25) * mm, "end": v(-5.43, 3.39) * mm});
            skArc(sketch, "E335", {"start": v(-5.43, 3.39) * mm, "mid": v(-5.29, 3.6) * mm, "end": v(-5.14, 3.82) * mm});
            skLineSegment(sketch, "E336", {"start": v(-5.14, 3.82) * mm, "end": v(-4.99, 3.8) * mm});
            skLineSegment(sketch, "E337", {"start": v(-4.99, 3.8) * mm, "end": v(-4.83, 3.8) * mm});
            skLineSegment(sketch, "E338", {"start": v(-4.83, 3.8) * mm, "end": v(-4.68, 3.77) * mm});
            skLineSegment(sketch, "E339", {"start": v(-4.68, 3.77) * mm, "end": v(-4.54, 3.74) * mm});
            skLineSegment(sketch, "E340", {"start": v(-4.54, 3.74) * mm, "end": v(-4.42, 3.71) * mm});
            skLineSegment(sketch, "E341", {"start": v(-4.42, 3.71) * mm, "end": v(-4.31, 3.68) * mm});
            skLineSegment(sketch, "E342", {"start": v(-4.31, 3.68) * mm, "end": v(-4.22, 3.64) * mm});
            skLineSegment(sketch, "E343", {"start": v(-4.22, 3.64) * mm, "end": v(-4.14, 3.61) * mm});
            skLineSegment(sketch, "E344", {"start": v(-4.14, 3.61) * mm, "end": v(-4.08, 3.58) * mm});
            skLineSegment(sketch, "E345", {"start": v(-4.08, 3.58) * mm, "end": v(-4.02, 3.55) * mm});
            skLineSegment(sketch, "E346", {"start": v(-4.02, 3.55) * mm, "end": v(-3.98, 3.53) * mm});
            skLineSegment(sketch, "E347", {"start": v(-3.98, 3.53) * mm, "end": v(-3.96, 3.5) * mm});
            skLineSegment(sketch, "E348", {"start": v(-3.96, 3.5) * mm, "end": v(-3.94, 3.5) * mm});
            skLineSegment(sketch, "E349", {"start": v(-3.94, 3.5) * mm, "end": v(-3.94, 3.5) * mm});
            skLineSegment(sketch, "E350", {"start": v(-3.94, 3.5) * mm, "end": v(-3.5, 3.1) * mm});
            skArc(sketch, "E351", {"start": v(-3.5, 3.1) * mm, "mid": v(-3.18, 3.43) * mm, "end": v(-2.83, 3.72) * mm});
            skLineSegment(sketch, "E352", {"start": v(-2.83, 3.72) * mm, "end": v(-3.19, 4.19) * mm});
            skLineSegment(sketch, "E353", {"start": v(-3.19, 4.19) * mm, "end": v(-3.2, 4.2) * mm});
            skLineSegment(sketch, "E354", {"start": v(-3.2, 4.2) * mm, "end": v(-3.2, 4.2) * mm});
            skLineSegment(sketch, "E355", {"start": v(-3.2, 4.2) * mm, "end": v(-3.22, 4.24) * mm});
            skLineSegment(sketch, "E356", {"start": v(-3.22, 4.24) * mm, "end": v(-3.24, 4.28) * mm});
            skLineSegment(sketch, "E357", {"start": v(-3.24, 4.28) * mm, "end": v(-3.26, 4.33) * mm});
            skLineSegment(sketch, "E358", {"start": v(-3.26, 4.33) * mm, "end": v(-3.3, 4.4) * mm});
            skLineSegment(sketch, "E359", {"start": v(-3.3, 4.4) * mm, "end": v(-3.32, 4.48) * mm});
            skLineSegment(sketch, "E360", {"start": v(-3.32, 4.48) * mm, "end": v(-3.35, 4.58) * mm});
            skLineSegment(sketch, "E361", {"start": v(-3.35, 4.58) * mm, "end": v(-3.37, 4.68) * mm});
            skLineSegment(sketch, "E362", {"start": v(-3.37, 4.68) * mm, "end": v(-3.4, 4.8) * mm});
            skLineSegment(sketch, "E363", {"start": v(-3.4, 4.8) * mm, "end": v(-3.4, 4.94) * mm});
            skLineSegment(sketch, "E364", {"start": v(-3.4, 4.94) * mm, "end": v(-3.42, 5.1) * mm});
            skLineSegment(sketch, "E365", {"start": v(-3.42, 5.1) * mm, "end": v(-3.42, 5.26) * mm});
            skLineSegment(sketch, "E366", {"start": v(-3.42, 5.26) * mm, "end": v(-3.42, 5.4) * mm});
            skArc(sketch, "E367", {"start": v(-3.42, 5.4) * mm, "mid": v(-3.2, 5.54) * mm, "end": v(-2.97, 5.67) * mm});
            skLineSegment(sketch, "E368", {"start": v(-2.97, 5.67) * mm, "end": v(-2.84, 5.6) * mm});
            skLineSegment(sketch, "E369", {"start": v(-2.84, 5.6) * mm, "end": v(-2.7, 5.5) * mm});
            skLineSegment(sketch, "E370", {"start": v(-2.7, 5.5) * mm, "end": v(-2.58, 5.42) * mm});
            skLineSegment(sketch, "E371", {"start": v(-2.58, 5.42) * mm, "end": v(-2.47, 5.34) * mm});
            skLineSegment(sketch, "E372", {"start": v(-2.47, 5.34) * mm, "end": v(-2.37, 5.26) * mm});
            skLineSegment(sketch, "E373", {"start": v(-2.37, 5.26) * mm, "end": v(-2.29, 5.18) * mm});
            skLineSegment(sketch, "E374", {"start": v(-2.29, 5.18) * mm, "end": v(-2.22, 5.11) * mm});
            skLineSegment(sketch, "E375", {"start": v(-2.22, 5.11) * mm, "end": v(-2.16, 5.05) * mm});
            skLineSegment(sketch, "E376", {"start": v(-2.16, 5.05) * mm, "end": v(-2.12, 5) * mm});
            skLineSegment(sketch, "E377", {"start": v(-2.12, 5) * mm, "end": v(-2.08, 4.94) * mm});
            skLineSegment(sketch, "E378", {"start": v(-2.08, 4.94) * mm, "end": v(-2.06, 4.9) * mm});
            skLineSegment(sketch, "E379", {"start": v(-2.06, 4.9) * mm, "end": v(-2.04, 4.88) * mm});
            skLineSegment(sketch, "E380", {"start": v(-2.04, 4.88) * mm, "end": v(-2.03, 4.86) * mm});
            skLineSegment(sketch, "E381", {"start": v(-2.03, 4.86) * mm, "end": v(-2.03, 4.85) * mm});
            skLineSegment(sketch, "E382", {"start": v(-2.03, 4.85) * mm, "end": v(-1.8, 4.31) * mm});
            skArc(sketch, "E383", {"start": v(-1.8, 4.31) * mm, "mid": v(-1.38, 4.47) * mm, "end": v(-0.94, 4.58) * mm});
            skLineSegment(sketch, "E384", {"start": v(-0.94, 4.58) * mm, "end": v(-1.06, 5.16) * mm});
            skLineSegment(sketch, "E385", {"start": v(-1.06, 5.16) * mm, "end": v(-1.06, 5.16) * mm});
            skLineSegment(sketch, "E386", {"start": v(-1.06, 5.16) * mm, "end": v(-1.06, 5.18) * mm});
            skLineSegment(sketch, "E387", {"start": v(-1.06, 5.18) * mm, "end": v(-1.06, 5.21) * mm});
            skLineSegment(sketch, "E388", {"start": v(-1.06, 5.21) * mm, "end": v(-1.06, 5.26) * mm});
            skLineSegment(sketch, "E389", {"start": v(-1.06, 5.26) * mm, "end": v(-1.06, 5.32) * mm});
            skLineSegment(sketch, "E390", {"start": v(-1.06, 5.32) * mm, "end": v(-1.06, 5.4) * mm});
            skLineSegment(sketch, "E391", {"start": v(-1.06, 5.4) * mm, "end": v(-1.05, 5.48) * mm});
            skLineSegment(sketch, "E392", {"start": v(-1.05, 5.48) * mm, "end": v(-1.03, 5.57) * mm});
            skLineSegment(sketch, "E393", {"start": v(-1.03, 5.57) * mm, "end": v(-1, 5.68) * mm});
            skLineSegment(sketch, "E394", {"start": v(-1, 5.68) * mm, "end": v(-0.97, 5.8) * mm});
            skLineSegment(sketch, "E395", {"start": v(-0.97, 5.8) * mm, "end": v(-0.93, 5.93) * mm});
            skLineSegment(sketch, "E396", {"start": v(-0.93, 5.93) * mm, "end": v(-0.87, 6.07) * mm});
            skLineSegment(sketch, "E397", {"start": v(-0.87, 6.07) * mm, "end": v(-0.8, 6.22) * mm});
            skLineSegment(sketch, "E398", {"start": v(-0.8, 6.22) * mm, "end": v(-0.74, 6.36) * mm});
            skArc(sketch, "E399", {"start": v(-0.74, 6.36) * mm, "mid": v(-0.48, 6.38) * mm, "end": v(-0.22, 6.4) * mm});
            skLineSegment(sketch, "E400", {"start": v(-0.22, 6.4) * mm, "end": v(-0.13, 6.27) * mm});
            skLineSegment(sketch, "E401", {"start": v(-0.13, 6.27) * mm, "end": v(-0.04, 6.14) * mm});
            skLineSegment(sketch, "E402", {"start": v(-0.04, 6.14) * mm, "end": v(0.03, 6) * mm});
            skLineSegment(sketch, "E403", {"start": v(0.03, 6) * mm, "end": v(0.1, 5.88) * mm});
            skLineSegment(sketch, "E404", {"start": v(0.1, 5.88) * mm, "end": v(0.15, 5.77) * mm});
            skLineSegment(sketch, "E405", {"start": v(0.15, 5.77) * mm, "end": v(0.19, 5.66) * mm});
            skLineSegment(sketch, "E406", {"start": v(0.19, 5.66) * mm, "end": v(0.22, 5.57) * mm});
            skLineSegment(sketch, "E407", {"start": v(0.22, 5.57) * mm, "end": v(0.24, 5.49) * mm});
            skLineSegment(sketch, "E408", {"start": v(0.24, 5.49) * mm, "end": v(0.26, 5.42) * mm});
            skLineSegment(sketch, "E409", {"start": v(0.26, 5.42) * mm, "end": v(0.27, 5.36) * mm});
            skLineSegment(sketch, "E410", {"start": v(0.27, 5.36) * mm, "end": v(0.27, 5.31) * mm});
            skLineSegment(sketch, "E411", {"start": v(0.27, 5.31) * mm, "end": v(0.28, 5.28) * mm});
            skLineSegment(sketch, "E412", {"start": v(0.28, 5.28) * mm, "end": v(0.28, 5.26) * mm});
            skLineSegment(sketch, "E413", {"start": v(0.28, 5.26) * mm, "end": v(0.28, 5.26) * mm});
            skLineSegment(sketch, "E414", {"start": v(0.28, 5.26) * mm, "end": v(0.24, 4.67) * mm});
            skArc(sketch, "E415", {"start": v(0.24, 4.67) * mm, "mid": v(0.7, 4.62) * mm, "end": v(1.14, 4.53) * mm});
            skLineSegment(sketch, "E416", {"start": v(1.14, 4.53) * mm, "end": v(1.29, 5.1) * mm});
            skLineSegment(sketch, "E417", {"start": v(1.29, 5.1) * mm, "end": v(1.29, 5.1) * mm});
            skLineSegment(sketch, "E418", {"start": v(1.29, 5.1) * mm, "end": v(1.3, 5.13) * mm});
            skLineSegment(sketch, "E419", {"start": v(1.3, 5.13) * mm, "end": v(1.3, 5.16) * mm});
            skLineSegment(sketch, "E420", {"start": v(1.3, 5.16) * mm, "end": v(1.32, 5.2) * mm});
            skLineSegment(sketch, "E421", {"start": v(1.32, 5.2) * mm, "end": v(1.35, 5.25) * mm});
            skLineSegment(sketch, "E422", {"start": v(1.35, 5.25) * mm, "end": v(1.39, 5.32) * mm});
            skLineSegment(sketch, "E423", {"start": v(1.39, 5.32) * mm, "end": v(1.43, 5.39) * mm});
            skLineSegment(sketch, "E424", {"start": v(1.43, 5.39) * mm, "end": v(1.5, 5.47) * mm});
            skLineSegment(sketch, "E425", {"start": v(1.5, 5.47) * mm, "end": v(1.56, 5.56) * mm});
            skLineSegment(sketch, "E426", {"start": v(1.56, 5.56) * mm, "end": v(1.64, 5.65) * mm});
            skLineSegment(sketch, "E427", {"start": v(1.64, 5.65) * mm, "end": v(1.74, 5.75) * mm});
            skLineSegment(sketch, "E428", {"start": v(1.74, 5.75) * mm, "end": v(1.85, 5.85) * mm});
            skLineSegment(sketch, "E429", {"start": v(1.85, 5.85) * mm, "end": v(1.98, 5.96) * mm});
            skLineSegment(sketch, "E430", {"start": v(1.98, 5.96) * mm, "end": v(2.1, 6.05) * mm});
            skArc(sketch, "E431", {"start": v(2.1, 6.05) * mm, "mid": v(2.34, 5.96) * mm, "end": v(2.58, 5.86) * mm});
            skLineSegment(sketch, "E432", {"start": v(2.58, 5.86) * mm, "end": v(2.6, 5.71) * mm});
            skLineSegment(sketch, "E433", {"start": v(2.6, 5.71) * mm, "end": v(2.62, 5.55) * mm});
            skLineSegment(sketch, "E434", {"start": v(2.62, 5.55) * mm, "end": v(2.63, 5.4) * mm});
            skLineSegment(sketch, "E435", {"start": v(2.63, 5.4) * mm, "end": v(2.64, 5.26) * mm});
            skLineSegment(sketch, "E436", {"start": v(2.64, 5.26) * mm, "end": v(2.63, 5.13) * mm});
            skLineSegment(sketch, "E437", {"start": v(2.63, 5.13) * mm, "end": v(2.63, 5.02) * mm});
            skLineSegment(sketch, "E438", {"start": v(2.63, 5.02) * mm, "end": v(2.61, 4.92) * mm});
            skLineSegment(sketch, "E439", {"start": v(2.61, 4.92) * mm, "end": v(2.6, 4.84) * mm});
            skLineSegment(sketch, "E440", {"start": v(2.6, 4.84) * mm, "end": v(2.58, 4.77) * mm});
            skLineSegment(sketch, "E441", {"start": v(2.58, 4.77) * mm, "end": v(2.57, 4.71) * mm});
            skLineSegment(sketch, "E442", {"start": v(2.57, 4.71) * mm, "end": v(2.55, 4.67) * mm});
            skLineSegment(sketch, "E443", {"start": v(2.55, 4.67) * mm, "end": v(2.54, 4.64) * mm});
            skLineSegment(sketch, "E444", {"start": v(2.54, 4.64) * mm, "end": v(2.53, 4.62) * mm});
            skLineSegment(sketch, "E445", {"start": v(2.53, 4.62) * mm, "end": v(2.53, 4.62) * mm});
            skLineSegment(sketch, "E446", {"start": v(2.53, 4.62) * mm, "end": v(2.25, 4.1) * mm});
            skArc(sketch, "E447", {"start": v(2.25, 4.1) * mm, "mid": v(2.63, 3.86) * mm, "end": v(3, 3.59) * mm});
            skLineSegment(sketch, "E448", {"start": v(18.3, 15.34) * mm, "end": v(18.43, 15.4) * mm});
            skLineSegment(sketch, "E449", {"start": v(18.43, 15.4) * mm, "end": v(18.72, 15.54) * mm});
            skLineSegment(sketch, "E450", {"start": v(18.72, 15.54) * mm, "end": v(19.07, 15.68) * mm});
            skLineSegment(sketch, "E451", {"start": v(19.07, 15.68) * mm, "end": v(19.49, 15.82) * mm});
            skLineSegment(sketch, "E452", {"start": v(19.49, 15.82) * mm, "end": v(19.96, 15.96) * mm});
            skLineSegment(sketch, "E453", {"start": v(19.96, 15.96) * mm, "end": v(20.01, 15.97) * mm});
            skArc(sketch, "E454", {"start": v(20.01, 15.97) * mm, "mid": v(20.2, 15.72) * mm, "end": v(20.4, 15.47) * mm});
            skLineSegment(sketch, "E455", {"start": v(20.4, 15.47) * mm, "end": v(20.38, 15.42) * mm});
            skLineSegment(sketch, "E456", {"start": v(20.38, 15.42) * mm, "end": v(20.13, 15) * mm});
            skLineSegment(sketch, "E457", {"start": v(20.13, 15) * mm, "end": v(19.9, 14.63) * mm});
            skLineSegment(sketch, "E458", {"start": v(19.9, 14.63) * mm, "end": v(19.67, 14.32) * mm});
            skLineSegment(sketch, "E459", {"start": v(19.67, 14.32) * mm, "end": v(19.47, 14.07) * mm});
            skLineSegment(sketch, "E460", {"start": v(19.47, 14.07) * mm, "end": v(19.37, 13.96) * mm});
            skArc(sketch, "E461", {"start": v(19.37, 13.96) * mm, "mid": v(19.56, 13.69) * mm, "end": v(19.75, 13.41) * mm});
            skLineSegment(sketch, "E462", {"start": v(19.75, 13.41) * mm, "end": v(19.9, 13.47) * mm});
            skLineSegment(sketch, "E463", {"start": v(19.9, 13.47) * mm, "end": v(20.2, 13.57) * mm});
            skLineSegment(sketch, "E464", {"start": v(20.2, 13.57) * mm, "end": v(20.56, 13.67) * mm});
            skLineSegment(sketch, "E465", {"start": v(20.56, 13.67) * mm, "end": v(20.99, 13.77) * mm});
            skLineSegment(sketch, "E466", {"start": v(20.99, 13.77) * mm, "end": v(21.47, 13.85) * mm});
            skLineSegment(sketch, "E467", {"start": v(21.47, 13.85) * mm, "end": v(21.52, 13.86) * mm});
            skArc(sketch, "E468", {"start": v(21.52, 13.86) * mm, "mid": v(21.7, 13.6) * mm, "end": v(21.86, 13.32) * mm});
            skLineSegment(sketch, "E469", {"start": v(21.86, 13.32) * mm, "end": v(21.83, 13.28) * mm});
            skLineSegment(sketch, "E470", {"start": v(21.83, 13.28) * mm, "end": v(21.54, 12.88) * mm});
            skLineSegment(sketch, "E471", {"start": v(21.54, 12.88) * mm, "end": v(21.27, 12.54) * mm});
            skLineSegment(sketch, "E472", {"start": v(21.27, 12.54) * mm, "end": v(21.02, 12.26) * mm});
            skLineSegment(sketch, "E473", {"start": v(21.02, 12.26) * mm, "end": v(20.8, 12.03) * mm});
            skLineSegment(sketch, "E474", {"start": v(20.8, 12.03) * mm, "end": v(20.68, 11.93) * mm});
            skArc(sketch, "E475", {"start": v(20.68, 11.93) * mm, "mid": v(20.85, 11.64) * mm, "end": v(21, 11.34) * mm});
            skLineSegment(sketch, "E476", {"start": v(21, 11.34) * mm, "end": v(21.15, 11.38) * mm});
            skLineSegment(sketch, "E477", {"start": v(21.15, 11.38) * mm, "end": v(21.46, 11.46) * mm});
            skLineSegment(sketch, "E478", {"start": v(21.46, 11.46) * mm, "end": v(21.84, 11.52) * mm});
            skLineSegment(sketch, "E479", {"start": v(21.84, 11.52) * mm, "end": v(22.27, 11.57) * mm});
            skLineSegment(sketch, "E480", {"start": v(22.27, 11.57) * mm, "end": v(22.77, 11.61) * mm});
            skLineSegment(sketch, "E481", {"start": v(22.77, 11.61) * mm, "end": v(22.81, 11.61) * mm});
            skArc(sketch, "E482", {"start": v(22.81, 11.61) * mm, "mid": v(22.96, 11.33) * mm, "end": v(23.1, 11.05) * mm});
            skLineSegment(sketch, "E483", {"start": v(23.1, 11.05) * mm, "end": v(23.06, 11) * mm});
            skLineSegment(sketch, "E484", {"start": v(23.06, 11) * mm, "end": v(22.73, 10.64) * mm});
            skLineSegment(sketch, "E485", {"start": v(22.73, 10.64) * mm, "end": v(22.43, 10.33) * mm});
            skLineSegment(sketch, "E486", {"start": v(22.43, 10.33) * mm, "end": v(22.15, 10.07) * mm});
            skLineSegment(sketch, "E487", {"start": v(22.15, 10.07) * mm, "end": v(21.9, 9.86) * mm});
            skLineSegment(sketch, "E488", {"start": v(21.9, 9.86) * mm, "end": v(21.78, 9.77) * mm});
            skArc(sketch, "E489", {"start": v(21.78, 9.77) * mm, "mid": v(21.92, 9.47) * mm, "end": v(22.05, 9.16) * mm});
            skLineSegment(sketch, "E490", {"start": v(22.05, 9.16) * mm, "end": v(22.2, 9.19) * mm});
            skLineSegment(sketch, "E491", {"start": v(22.2, 9.19) * mm, "end": v(22.51, 9.23) * mm});
            skLineSegment(sketch, "E492", {"start": v(22.51, 9.23) * mm, "end": v(22.9, 9.25) * mm});
            skLineSegment(sketch, "E493", {"start": v(22.9, 9.25) * mm, "end": v(23.33, 9.26) * mm});
            skLineSegment(sketch, "E494", {"start": v(23.33, 9.26) * mm, "end": v(23.82, 9.25) * mm});
            skLineSegment(sketch, "E495", {"start": v(23.82, 9.25) * mm, "end": v(23.87, 9.24) * mm});
            skArc(sketch, "E496", {"start": v(23.87, 9.24) * mm, "mid": v(23.98, 8.95) * mm, "end": v(24.1, 8.65) * mm});
            skLineSegment(sketch, "E497", {"start": v(24.1, 8.65) * mm, "end": v(24.06, 8.62) * mm});
            skLineSegment(sketch, "E498", {"start": v(24.06, 8.62) * mm, "end": v(23.7, 8.28) * mm});
            skLineSegment(sketch, "E499", {"start": v(23.7, 8.28) * mm, "end": v(23.36, 8) * mm});
            skLineSegment(sketch, "E500", {"start": v(23.36, 8) * mm, "end": v(23.05, 7.78) * mm});
            skLineSegment(sketch, "E501", {"start": v(23.05, 7.78) * mm, "end": v(22.79, 7.6) * mm});
            skLineSegment(sketch, "E502", {"start": v(22.79, 7.6) * mm, "end": v(22.66, 7.52) * mm});
            skArc(sketch, "E503", {"start": v(22.66, 7.52) * mm, "mid": v(22.76, 7.2) * mm, "end": v(22.86, 6.88) * mm});
            skLineSegment(sketch, "E504", {"start": v(22.86, 6.88) * mm, "end": v(23.01, 6.9) * mm});
            skLineSegment(sketch, "E505", {"start": v(23.01, 6.9) * mm, "end": v(23.33, 6.9) * mm});
            skLineSegment(sketch, "E506", {"start": v(23.33, 6.9) * mm, "end": v(23.7, 6.89) * mm});
            skLineSegment(sketch, "E507", {"start": v(23.7, 6.89) * mm, "end": v(24.15, 6.85) * mm});
            skLineSegment(sketch, "E508", {"start": v(24.15, 6.85) * mm, "end": v(24.64, 6.8) * mm});
            skLineSegment(sketch, "E509", {"start": v(24.64, 6.8) * mm, "end": v(24.69, 6.78) * mm});
            skArc(sketch, "E510", {"start": v(24.69, 6.78) * mm, "mid": v(24.77, 6.48) * mm, "end": v(24.85, 6.17) * mm});
            skLineSegment(sketch, "E511", {"start": v(24.85, 6.17) * mm, "end": v(24.8, 6.14) * mm});
            skLineSegment(sketch, "E512", {"start": v(24.8, 6.14) * mm, "end": v(24.41, 5.84) * mm});
            skLineSegment(sketch, "E513", {"start": v(24.41, 5.84) * mm, "end": v(24.05, 5.6) * mm});
            skLineSegment(sketch, "E514", {"start": v(24.05, 5.6) * mm, "end": v(23.72, 5.4) * mm});
            skLineSegment(sketch, "E515", {"start": v(23.72, 5.4) * mm, "end": v(23.44, 5.25) * mm});
            skLineSegment(sketch, "E516", {"start": v(23.44, 5.25) * mm, "end": v(23.3, 5.19) * mm});
            skArc(sketch, "E517", {"start": v(23.3, 5.19) * mm, "mid": v(23.37, 4.86) * mm, "end": v(23.44, 4.54) * mm});
            skLineSegment(sketch, "E518", {"start": v(23.44, 4.54) * mm, "end": v(23.6, 4.53) * mm});
            skLineSegment(sketch, "E519", {"start": v(23.6, 4.53) * mm, "end": v(23.9, 4.5) * mm});
            skLineSegment(sketch, "E520", {"start": v(23.9, 4.5) * mm, "end": v(24.29, 4.46) * mm});
            skLineSegment(sketch, "E521", {"start": v(24.29, 4.46) * mm, "end": v(24.72, 4.38) * mm});
            skLineSegment(sketch, "E522", {"start": v(24.72, 4.38) * mm, "end": v(25.2, 4.26) * mm});
            skLineSegment(sketch, "E523", {"start": v(25.2, 4.26) * mm, "end": v(25.24, 4.25) * mm});
            skArc(sketch, "E524", {"start": v(25.24, 4.25) * mm, "mid": v(25.3, 3.94) * mm, "end": v(25.34, 3.62) * mm});
            skLineSegment(sketch, "E525", {"start": v(25.34, 3.62) * mm, "end": v(25.3, 3.6) * mm});
            skLineSegment(sketch, "E526", {"start": v(25.3, 3.6) * mm, "end": v(24.88, 3.34) * mm});
            skLineSegment(sketch, "E527", {"start": v(24.88, 3.34) * mm, "end": v(24.5, 3.14) * mm});
            skLineSegment(sketch, "E528", {"start": v(24.5, 3.14) * mm, "end": v(24.15, 2.98) * mm});
            skLineSegment(sketch, "E529", {"start": v(24.15, 2.98) * mm, "end": v(23.85, 2.85) * mm});
            skLineSegment(sketch, "E530", {"start": v(23.85, 2.85) * mm, "end": v(23.7, 2.8) * mm});
            skArc(sketch, "E531", {"start": v(23.7, 2.8) * mm, "mid": v(23.75, 2.47) * mm, "end": v(23.78, 2.14) * mm});
            skLineSegment(sketch, "E532", {"start": v(23.78, 2.14) * mm, "end": v(23.93, 2.12) * mm});
            skLineSegment(sketch, "E533", {"start": v(23.93, 2.12) * mm, "end": v(24.24, 2.06) * mm});
            skLineSegment(sketch, "E534", {"start": v(24.24, 2.06) * mm, "end": v(24.61, 1.98) * mm});
            skLineSegment(sketch, "E535", {"start": v(24.61, 1.98) * mm, "end": v(25.03, 1.85) * mm});
            skLineSegment(sketch, "E536", {"start": v(25.03, 1.85) * mm, "end": v(25.5, 1.7) * mm});
            skLineSegment(sketch, "E537", {"start": v(25.5, 1.7) * mm, "end": v(25.55, 1.67) * mm});
            skArc(sketch, "E538", {"start": v(25.55, 1.67) * mm, "mid": v(25.56, 1.36) * mm, "end": v(25.58, 1.04) * mm});
            skLineSegment(sketch, "E539", {"start": v(25.58, 1.04) * mm, "end": v(25.53, 1.02) * mm});
            skLineSegment(sketch, "E540", {"start": v(25.53, 1.02) * mm, "end": v(25.09, 0.8) * mm});
            skLineSegment(sketch, "E541", {"start": v(25.09, 0.8) * mm, "end": v(24.68, 0.64) * mm});
            skLineSegment(sketch, "E542", {"start": v(24.68, 0.64) * mm, "end": v(24.32, 0.52) * mm});
            skLineSegment(sketch, "E543", {"start": v(24.32, 0.52) * mm, "end": v(24.02, 0.43) * mm});
            skLineSegment(sketch, "E544", {"start": v(24.02, 0.43) * mm, "end": v(23.87, 0.4) * mm});
            skArc(sketch, "E545", {"start": v(23.87, 0.4) * mm, "mid": v(23.87, 0.06) * mm, "end": v(23.87, -0.28) * mm});
            skLineSegment(sketch, "E546", {"start": v(23.87, -0.28) * mm, "end": v(24.02, -0.31) * mm});
            skLineSegment(sketch, "E547", {"start": v(24.02, -0.31) * mm, "end": v(24.33, -0.4) * mm});
            skLineSegment(sketch, "E548", {"start": v(24.33, -0.4) * mm, "end": v(24.68, -0.52) * mm});
            skLineSegment(sketch, "E549", {"start": v(24.68, -0.52) * mm, "end": v(25.1, -0.69) * mm});
            skLineSegment(sketch, "E550", {"start": v(25.1, -0.69) * mm, "end": v(25.54, -0.9) * mm});
            skLineSegment(sketch, "E551", {"start": v(25.54, -0.9) * mm, "end": v(25.58, -0.92) * mm});
            skArc(sketch, "E552", {"start": v(25.58, -0.92) * mm, "mid": v(25.57, -1.24) * mm, "end": v(25.55, -1.55) * mm});
            skLineSegment(sketch, "E553", {"start": v(25.55, -1.55) * mm, "end": v(25.5, -1.57) * mm});
            skLineSegment(sketch, "E554", {"start": v(25.5, -1.57) * mm, "end": v(25.04, -1.73) * mm});
            skLineSegment(sketch, "E555", {"start": v(25.04, -1.73) * mm, "end": v(24.62, -1.86) * mm});
            skLineSegment(sketch, "E556", {"start": v(24.62, -1.86) * mm, "end": v(24.25, -1.95) * mm});
            skLineSegment(sketch, "E557", {"start": v(24.25, -1.95) * mm, "end": v(23.94, -2) * mm});
            skLineSegment(sketch, "E558", {"start": v(23.94, -2) * mm, "end": v(23.79, -2.03) * mm});
            skArc(sketch, "E559", {"start": v(23.79, -2.03) * mm, "mid": v(23.76, -2.36) * mm, "end": v(23.72, -2.69) * mm});
            skLineSegment(sketch, "E560", {"start": v(23.72, -2.69) * mm, "end": v(23.86, -2.74) * mm});
            skLineSegment(sketch, "E561", {"start": v(23.86, -2.74) * mm, "end": v(24.16, -2.86) * mm});
            skLineSegment(sketch, "E562", {"start": v(24.16, -2.86) * mm, "end": v(24.5, -3.02) * mm});
            skLineSegment(sketch, "E563", {"start": v(24.5, -3.02) * mm, "end": v(24.9, -3.22) * mm});
            skLineSegment(sketch, "E564", {"start": v(24.9, -3.22) * mm, "end": v(25.32, -3.48) * mm});
            skLineSegment(sketch, "E565", {"start": v(25.32, -3.48) * mm, "end": v(25.36, -3.5) * mm});
            skArc(sketch, "E566", {"start": v(25.36, -3.5) * mm, "mid": v(25.31, -3.82) * mm, "end": v(25.27, -4.13) * mm});
            skLineSegment(sketch, "E567", {"start": v(25.27, -4.13) * mm, "end": v(25.22, -4.14) * mm});
            skLineSegment(sketch, "E568", {"start": v(25.22, -4.14) * mm, "end": v(24.74, -4.26) * mm});
            skLineSegment(sketch, "E569", {"start": v(24.74, -4.26) * mm, "end": v(24.3, -4.34) * mm});
            skLineSegment(sketch, "E570", {"start": v(24.3, -4.34) * mm, "end": v(23.93, -4.39) * mm});
            skLineSegment(sketch, "E571", {"start": v(23.93, -4.39) * mm, "end": v(23.61, -4.42) * mm});
            skLineSegment(sketch, "E572", {"start": v(23.61, -4.42) * mm, "end": v(23.46, -4.42) * mm});
            skArc(sketch, "E573", {"start": v(23.46, -4.42) * mm, "mid": v(23.4, -4.75) * mm, "end": v(23.33, -5.08) * mm});
            skLineSegment(sketch, "E574", {"start": v(23.33, -5.08) * mm, "end": v(23.47, -5.14) * mm});
            skLineSegment(sketch, "E575", {"start": v(23.47, -5.14) * mm, "end": v(23.75, -5.29) * mm});
            skLineSegment(sketch, "E576", {"start": v(23.75, -5.29) * mm, "end": v(24.07, -5.48) * mm});
            skLineSegment(sketch, "E577", {"start": v(24.07, -5.48) * mm, "end": v(24.44, -5.72) * mm});
            skLineSegment(sketch, "E578", {"start": v(24.44, -5.72) * mm, "end": v(24.84, -6.02) * mm});
            skLineSegment(sketch, "E579", {"start": v(24.84, -6.02) * mm, "end": v(24.87, -6.05) * mm});
            skArc(sketch, "E580", {"start": v(24.87, -6.05) * mm, "mid": v(24.8, -6.36) * mm, "end": v(24.72, -6.66) * mm});
            skLineSegment(sketch, "E581", {"start": v(24.72, -6.66) * mm, "end": v(24.67, -6.67) * mm});
            skLineSegment(sketch, "E582", {"start": v(24.67, -6.67) * mm, "end": v(24.18, -6.74) * mm});
            skLineSegment(sketch, "E583", {"start": v(24.18, -6.74) * mm, "end": v(23.74, -6.77) * mm});
            skLineSegment(sketch, "E584", {"start": v(23.74, -6.77) * mm, "end": v(23.36, -6.79) * mm});
            skLineSegment(sketch, "E585", {"start": v(23.36, -6.79) * mm, "end": v(23.04, -6.78) * mm});
            skLineSegment(sketch, "E586", {"start": v(23.04, -6.78) * mm, "end": v(22.9, -6.77) * mm});
            skArc(sketch, "E587", {"start": v(22.9, -6.77) * mm, "mid": v(22.8, -7.1) * mm, "end": v(22.7, -7.41) * mm});
            skLineSegment(sketch, "E588", {"start": v(22.7, -7.41) * mm, "end": v(22.82, -7.49) * mm});
            skLineSegment(sketch, "E589", {"start": v(22.82, -7.49) * mm, "end": v(23.1, -7.67) * mm});
            skLineSegment(sketch, "E590", {"start": v(23.1, -7.67) * mm, "end": v(23.4, -7.9) * mm});
            skLineSegment(sketch, "E591", {"start": v(23.4, -7.9) * mm, "end": v(23.73, -8.17) * mm});
            skLineSegment(sketch, "E592", {"start": v(23.73, -8.17) * mm, "end": v(24.1, -8.5) * mm});
            skLineSegment(sketch, "E593", {"start": v(24.1, -8.5) * mm, "end": v(24.14, -8.54) * mm});
            skArc(sketch, "E594", {"start": v(24.14, -8.54) * mm, "mid": v(24.03, -8.83) * mm, "end": v(23.92, -9.13) * mm});
            skLineSegment(sketch, "E595", {"start": v(23.92, -9.13) * mm, "end": v(23.87, -9.13) * mm});
            skLineSegment(sketch, "E596", {"start": v(23.87, -9.13) * mm, "end": v(23.37, -9.15) * mm});
            skLineSegment(sketch, "E597", {"start": v(23.37, -9.15) * mm, "end": v(22.94, -9.14) * mm});
            skLineSegment(sketch, "E598", {"start": v(22.94, -9.14) * mm, "end": v(22.56, -9.12) * mm});
            skLineSegment(sketch, "E599", {"start": v(22.56, -9.12) * mm, "end": v(22.24, -9.08) * mm});
            skLineSegment(sketch, "E600", {"start": v(22.24, -9.08) * mm, "end": v(22.1, -9.05) * mm});
            skArc(sketch, "E601", {"start": v(22.1, -9.05) * mm, "mid": v(21.96, -9.36) * mm, "end": v(21.83, -9.67) * mm});
            skLineSegment(sketch, "E602", {"start": v(21.83, -9.67) * mm, "end": v(21.95, -9.76) * mm});
            skLineSegment(sketch, "E603", {"start": v(21.95, -9.76) * mm, "end": v(22.2, -9.96) * mm});
            skLineSegment(sketch, "E604", {"start": v(22.2, -9.96) * mm, "end": v(22.48, -10.22) * mm});
            skLineSegment(sketch, "E605", {"start": v(22.48, -10.22) * mm, "end": v(22.79, -10.53) * mm});
            skLineSegment(sketch, "E606", {"start": v(22.79, -10.53) * mm, "end": v(23.12, -10.9) * mm});
            skLineSegment(sketch, "E607", {"start": v(23.12, -10.9) * mm, "end": v(23.15, -10.93) * mm});
            skArc(sketch, "E608", {"start": v(23.15, -10.93) * mm, "mid": v(23.01, -11.22) * mm, "end": v(22.87, -11.5) * mm});
            skLineSegment(sketch, "E609", {"start": v(22.87, -11.5) * mm, "end": v(22.82, -11.5) * mm});
            skLineSegment(sketch, "E610", {"start": v(22.82, -11.5) * mm, "end": v(22.33, -11.47) * mm});
            skLineSegment(sketch, "E611", {"start": v(22.33, -11.47) * mm, "end": v(21.9, -11.42) * mm});
            skLineSegment(sketch, "E612", {"start": v(21.9, -11.42) * mm, "end": v(21.52, -11.35) * mm});
            skLineSegment(sketch, "E613", {"start": v(21.52, -11.35) * mm, "end": v(21.2, -11.28) * mm});
            skLineSegment(sketch, "E614", {"start": v(21.2, -11.28) * mm, "end": v(21.06, -11.24) * mm});
            skArc(sketch, "E615", {"start": v(21.06, -11.24) * mm, "mid": v(20.9, -11.54) * mm, "end": v(20.74, -11.83) * mm});
            skLineSegment(sketch, "E616", {"start": v(20.74, -11.83) * mm, "end": v(20.85, -11.93) * mm});
            skLineSegment(sketch, "E617", {"start": v(20.85, -11.93) * mm, "end": v(21.08, -12.16) * mm});
            skLineSegment(sketch, "E618", {"start": v(21.08, -12.16) * mm, "end": v(21.33, -12.44) * mm});
            skLineSegment(sketch, "E619", {"start": v(21.33, -12.44) * mm, "end": v(21.6, -12.78) * mm});
            skLineSegment(sketch, "E620", {"start": v(21.6, -12.78) * mm, "end": v(21.9, -13.18) * mm});
            skLineSegment(sketch, "E621", {"start": v(21.9, -13.18) * mm, "end": v(21.92, -13.22) * mm});
            skArc(sketch, "E622", {"start": v(21.92, -13.22) * mm, "mid": v(21.76, -13.49) * mm, "end": v(21.59, -13.76) * mm});
            skLineSegment(sketch, "E623", {"start": v(21.59, -13.76) * mm, "end": v(21.54, -13.75) * mm});
            skLineSegment(sketch, "E624", {"start": v(21.54, -13.75) * mm, "end": v(21.05, -13.67) * mm});
            skLineSegment(sketch, "E625", {"start": v(21.05, -13.67) * mm, "end": v(20.63, -13.57) * mm});
            skLineSegment(sketch, "E626", {"start": v(20.63, -13.57) * mm, "end": v(20.26, -13.47) * mm});
            skLineSegment(sketch, "E627", {"start": v(20.26, -13.47) * mm, "end": v(19.96, -13.37) * mm});
            skLineSegment(sketch, "E628", {"start": v(19.96, -13.37) * mm, "end": v(19.82, -13.32) * mm});
            skArc(sketch, "E629", {"start": v(19.82, -13.32) * mm, "mid": v(19.63, -13.6) * mm, "end": v(19.44, -13.86) * mm});
            skLineSegment(sketch, "E630", {"start": v(19.44, -13.86) * mm, "end": v(19.54, -13.98) * mm});
            skLineSegment(sketch, "E631", {"start": v(19.54, -13.98) * mm, "end": v(19.74, -14.23) * mm});
            skLineSegment(sketch, "E632", {"start": v(19.74, -14.23) * mm, "end": v(19.96, -14.53) * mm});
            skLineSegment(sketch, "E633", {"start": v(19.96, -14.53) * mm, "end": v(20.2, -14.9) * mm});
            skLineSegment(sketch, "E634", {"start": v(20.2, -14.9) * mm, "end": v(20.45, -15.33) * mm});
            skLineSegment(sketch, "E635", {"start": v(20.45, -15.33) * mm, "end": v(20.47, -15.37) * mm});
            skArc(sketch, "E636", {"start": v(20.47, -15.37) * mm, "mid": v(20.28, -15.62) * mm, "end": v(20.09, -15.87) * mm});
            skLineSegment(sketch, "E637", {"start": v(20.09, -15.87) * mm, "end": v(20.04, -15.86) * mm});
            skLineSegment(sketch, "E638", {"start": v(20.04, -15.86) * mm, "end": v(19.56, -15.73) * mm});
            skLineSegment(sketch, "E639", {"start": v(19.56, -15.73) * mm, "end": v(19.15, -15.59) * mm});
            skLineSegment(sketch, "E640", {"start": v(19.15, -15.59) * mm, "end": v(18.8, -15.45) * mm});
            skLineSegment(sketch, "E641", {"start": v(18.8, -15.45) * mm, "end": v(18.5, -15.32) * mm});
            skLineSegment(sketch, "E642", {"start": v(18.5, -15.32) * mm, "end": v(18.37, -15.25) * mm});
            skArc(sketch, "E643", {"start": v(18.37, -15.25) * mm, "mid": v(18.15, -15.5) * mm, "end": v(17.93, -15.76) * mm});
            skLineSegment(sketch, "E644", {"start": v(17.93, -15.76) * mm, "end": v(18.02, -15.88) * mm});
            skLineSegment(sketch, "E645", {"start": v(18.02, -15.88) * mm, "end": v(18.2, -16.15) * mm});
            skLineSegment(sketch, "E646", {"start": v(18.2, -16.15) * mm, "end": v(18.39, -16.48) * mm});
            skLineSegment(sketch, "E647", {"start": v(18.39, -16.48) * mm, "end": v(18.59, -16.87) * mm});
            skLineSegment(sketch, "E648", {"start": v(18.59, -16.87) * mm, "end": v(18.8, -17.32) * mm});
            skLineSegment(sketch, "E649", {"start": v(18.8, -17.32) * mm, "end": v(18.81, -17.36) * mm});
            skArc(sketch, "E650", {"start": v(18.81, -17.36) * mm, "mid": v(18.6, -17.6) * mm, "end": v(18.38, -17.82) * mm});
            skLineSegment(sketch, "E651", {"start": v(18.38, -17.82) * mm, "end": v(18.33, -17.8) * mm});
            skLineSegment(sketch, "E652", {"start": v(18.33, -17.8) * mm, "end": v(17.87, -17.63) * mm});
            skLineSegment(sketch, "E653", {"start": v(17.87, -17.63) * mm, "end": v(17.47, -17.45) * mm});
            skLineSegment(sketch, "E654", {"start": v(17.47, -17.45) * mm, "end": v(17.13, -17.27) * mm});
            skLineSegment(sketch, "E655", {"start": v(17.13, -17.27) * mm, "end": v(16.86, -17.11) * mm});
            skLineSegment(sketch, "E656", {"start": v(16.86, -17.11) * mm, "end": v(16.73, -17.03) * mm});
            skArc(sketch, "E657", {"start": v(16.73, -17.03) * mm, "mid": v(16.5, -17.26) * mm, "end": v(16.25, -17.5) * mm});
            skLineSegment(sketch, "E658", {"start": v(16.25, -17.5) * mm, "end": v(16.32, -17.62) * mm});
            skLineSegment(sketch, "E659", {"start": v(16.32, -17.62) * mm, "end": v(16.47, -17.9) * mm});
            skLineSegment(sketch, "E660", {"start": v(16.47, -17.9) * mm, "end": v(16.63, -18.25) * mm});
            skLineSegment(sketch, "E661", {"start": v(16.63, -18.25) * mm, "end": v(16.79, -18.66) * mm});
            skLineSegment(sketch, "E662", {"start": v(16.79, -18.66) * mm, "end": v(16.95, -19.13) * mm});
            skLineSegment(sketch, "E663", {"start": v(16.95, -19.13) * mm, "end": v(16.96, -19.18) * mm});
            skArc(sketch, "E664", {"start": v(16.96, -19.18) * mm, "mid": v(16.72, -19.38) * mm, "end": v(16.48, -19.59) * mm});
            skLineSegment(sketch, "E665", {"start": v(16.48, -19.59) * mm, "end": v(16.44, -19.57) * mm});
            skLineSegment(sketch, "E666", {"start": v(16.44, -19.57) * mm, "end": v(16, -19.34) * mm});
            skLineSegment(sketch, "E667", {"start": v(16, -19.34) * mm, "end": v(15.62, -19.12) * mm});
            skLineSegment(sketch, "E668", {"start": v(15.62, -19.12) * mm, "end": v(15.3, -18.92) * mm});
            skLineSegment(sketch, "E669", {"start": v(15.3, -18.92) * mm, "end": v(15.04, -18.73) * mm});
            skLineSegment(sketch, "E670", {"start": v(15.04, -18.73) * mm, "end": v(14.92, -18.64) * mm});
            skArc(sketch, "E671", {"start": v(14.92, -18.64) * mm, "mid": v(14.66, -18.84) * mm, "end": v(14.4, -19.05) * mm});
            skLineSegment(sketch, "E672", {"start": v(14.4, -19.05) * mm, "end": v(14.46, -19.18) * mm});
            skLineSegment(sketch, "E673", {"start": v(14.46, -19.18) * mm, "end": v(14.57, -19.48) * mm});
            skLineSegment(sketch, "E674", {"start": v(14.57, -19.48) * mm, "end": v(14.7, -19.84) * mm});
            skLineSegment(sketch, "E675", {"start": v(14.7, -19.84) * mm, "end": v(14.81, -20.26) * mm});
            skLineSegment(sketch, "E676", {"start": v(14.81, -20.26) * mm, "end": v(14.92, -20.74) * mm});
            skLineSegment(sketch, "E677", {"start": v(14.92, -20.74) * mm, "end": v(14.93, -20.8) * mm});
            skArc(sketch, "E678", {"start": v(14.93, -20.8) * mm, "mid": v(14.68, -20.98) * mm, "end": v(14.41, -21.16) * mm});
            skLineSegment(sketch, "E679", {"start": v(14.41, -21.16) * mm, "end": v(14.37, -21.13) * mm});
            skLineSegment(sketch, "E680", {"start": v(14.37, -21.13) * mm, "end": v(13.96, -20.86) * mm});
            skLineSegment(sketch, "E681", {"start": v(13.96, -20.86) * mm, "end": v(13.6, -20.6) * mm});
            skLineSegment(sketch, "E682", {"start": v(13.6, -20.6) * mm, "end": v(13.3, -20.37) * mm});
            skLineSegment(sketch, "E683", {"start": v(13.3, -20.37) * mm, "end": v(13.07, -20.16) * mm});
            skLineSegment(sketch, "E684", {"start": v(13.07, -20.16) * mm, "end": v(12.96, -20.05) * mm});
            skArc(sketch, "E685", {"start": v(12.96, -20.05) * mm, "mid": v(12.68, -20.23) * mm, "end": v(12.4, -20.4) * mm});
            skLineSegment(sketch, "E686", {"start": v(12.4, -20.4) * mm, "end": v(12.44, -20.55) * mm});
            skLineSegment(sketch, "E687", {"start": v(12.44, -20.55) * mm, "end": v(12.53, -20.86) * mm});
            skLineSegment(sketch, "E688", {"start": v(12.53, -20.86) * mm, "end": v(12.61, -21.23) * mm});
            skLineSegment(sketch, "E689", {"start": v(12.61, -21.23) * mm, "end": v(12.69, -21.66) * mm});
            skLineSegment(sketch, "E690", {"start": v(12.69, -21.66) * mm, "end": v(12.75, -22.15) * mm});
            skLineSegment(sketch, "E691", {"start": v(12.75, -22.15) * mm, "end": v(12.75, -22.2) * mm});
            skArc(sketch, "E692", {"start": v(12.75, -22.2) * mm, "mid": v(12.48, -22.35) * mm, "end": v(12.2, -22.5) * mm});
            skLineSegment(sketch, "E693", {"start": v(12.2, -22.5) * mm, "end": v(12.16, -22.48) * mm});
            skLineSegment(sketch, "E694", {"start": v(12.16, -22.48) * mm, "end": v(11.77, -22.17) * mm});
            skLineSegment(sketch, "E695", {"start": v(11.77, -22.17) * mm, "end": v(11.45, -21.88) * mm});
            skLineSegment(sketch, "E696", {"start": v(11.45, -21.88) * mm, "end": v(11.18, -21.61) * mm});
            skLineSegment(sketch, "E697", {"start": v(11.18, -21.61) * mm, "end": v(10.96, -21.38) * mm});
            skLineSegment(sketch, "E698", {"start": v(10.96, -21.38) * mm, "end": v(10.86, -21.26) * mm});
            skArc(sketch, "E699", {"start": v(10.86, -21.26) * mm, "mid": v(10.57, -21.4) * mm, "end": v(10.27, -21.55) * mm});
            skLineSegment(sketch, "E700", {"start": v(10.27, -21.55) * mm, "end": v(10.3, -21.7) * mm});
            skLineSegment(sketch, "E701", {"start": v(10.3, -21.7) * mm, "end": v(10.35, -22.02) * mm});
            skLineSegment(sketch, "E702", {"start": v(10.35, -22.02) * mm, "end": v(10.4, -22.4) * mm});
            skLineSegment(sketch, "E703", {"start": v(10.4, -22.4) * mm, "end": v(10.43, -22.83) * mm});
            skLineSegment(sketch, "E704", {"start": v(10.43, -22.83) * mm, "end": v(10.44, -23.32) * mm});
            skLineSegment(sketch, "E705", {"start": v(10.44, -23.32) * mm, "end": v(10.44, -23.37) * mm});
            skArc(sketch, "E706", {"start": v(10.44, -23.37) * mm, "mid": v(10.15, -23.5) * mm, "end": v(9.86, -23.62) * mm});
            skLineSegment(sketch, "E707", {"start": v(9.86, -23.62) * mm, "end": v(9.82, -23.6) * mm});
            skLineSegment(sketch, "E708", {"start": v(9.82, -23.6) * mm, "end": v(9.47, -23.24) * mm});
            skLineSegment(sketch, "E709", {"start": v(9.47, -23.24) * mm, "end": v(9.18, -22.92) * mm});
            skLineSegment(sketch, "E710", {"start": v(9.18, -22.92) * mm, "end": v(8.93, -22.63) * mm});
            skLineSegment(sketch, "E711", {"start": v(8.93, -22.63) * mm, "end": v(8.74, -22.37) * mm});
            skLineSegment(sketch, "E712", {"start": v(8.74, -22.37) * mm, "end": v(8.66, -22.25) * mm});
            skArc(sketch, "E713", {"start": v(8.66, -22.25) * mm, "mid": v(8.35, -22.37) * mm, "end": v(8.03, -22.48) * mm});
            skLineSegment(sketch, "E714", {"start": v(8.03, -22.48) * mm, "end": v(8.05, -22.63) * mm});
            skLineSegment(sketch, "E715", {"start": v(8.05, -22.63) * mm, "end": v(8.07, -22.95) * mm});
            skLineSegment(sketch, "E716", {"start": v(8.07, -22.95) * mm, "end": v(8.08, -23.33) * mm});
            skLineSegment(sketch, "E717", {"start": v(8.08, -23.33) * mm, "end": v(8.07, -23.77) * mm});
            skLineSegment(sketch, "E718", {"start": v(8.07, -23.77) * mm, "end": v(8.03, -24.26) * mm});
            skLineSegment(sketch, "E719", {"start": v(8.03, -24.26) * mm, "end": v(8.02, -24.31) * mm});
            skArc(sketch, "E720", {"start": v(8.02, -24.31) * mm, "mid": v(7.72, -24.4) * mm, "end": v(7.42, -24.5) * mm});
            skLineSegment(sketch, "E721", {"start": v(7.42, -24.5) * mm, "end": v(7.39, -24.46) * mm});
            skLineSegment(sketch, "E722", {"start": v(7.39, -24.46) * mm, "end": v(7.07, -24.08) * mm});
            skLineSegment(sketch, "E723", {"start": v(7.07, -24.08) * mm, "end": v(6.8, -23.73) * mm});
            skLineSegment(sketch, "E724", {"start": v(6.8, -23.73) * mm, "end": v(6.6, -23.42) * mm});
            skLineSegment(sketch, "E725", {"start": v(6.6, -23.42) * mm, "end": v(6.43, -23.14) * mm});
            skLineSegment(sketch, "E726", {"start": v(6.43, -23.14) * mm, "end": v(6.36, -23.01) * mm});
            skArc(sketch, "E727", {"start": v(6.36, -23.01) * mm, "mid": v(6.04, -23.1) * mm, "end": v(5.72, -23.18) * mm});
            skLineSegment(sketch, "E728", {"start": v(5.72, -23.18) * mm, "end": v(5.72, -23.33) * mm});
            skLineSegment(sketch, "E729", {"start": v(5.72, -23.33) * mm, "end": v(5.7, -23.65) * mm});
            skLineSegment(sketch, "E730", {"start": v(5.7, -23.65) * mm, "end": v(5.68, -24.03) * mm});
            skLineSegment(sketch, "E731", {"start": v(5.68, -24.03) * mm, "end": v(5.62, -24.46) * mm});
            skLineSegment(sketch, "E732", {"start": v(5.62, -24.46) * mm, "end": v(5.53, -24.95) * mm});
            skLineSegment(sketch, "E733", {"start": v(5.53, -24.95) * mm, "end": v(5.52, -25) * mm});
            skArc(sketch, "E734", {"start": v(5.52, -25) * mm, "mid": v(5.21, -25.06) * mm, "end": v(4.9, -25.13) * mm});
            skLineSegment(sketch, "E735", {"start": v(4.9, -25.13) * mm, "end": v(4.87, -25.09) * mm});
            skLineSegment(sketch, "E736", {"start": v(4.87, -25.09) * mm, "end": v(4.6, -24.67) * mm});
            skLineSegment(sketch, "E737", {"start": v(4.6, -24.67) * mm, "end": v(4.37, -24.3) * mm});
            skLineSegment(sketch, "E738", {"start": v(4.37, -24.3) * mm, "end": v(4.2, -23.97) * mm});
            skLineSegment(sketch, "E739", {"start": v(4.2, -23.97) * mm, "end": v(4.06, -23.68) * mm});
            skLineSegment(sketch, "E740", {"start": v(4.06, -23.68) * mm, "end": v(4, -23.54) * mm});
            skArc(sketch, "E741", {"start": v(4, -23.54) * mm, "mid": v(3.67, -23.6) * mm, "end": v(3.34, -23.64) * mm});
            skLineSegment(sketch, "E742", {"start": v(3.34, -23.64) * mm, "end": v(3.33, -23.79) * mm});
            skLineSegment(sketch, "E743", {"start": v(3.33, -23.79) * mm, "end": v(3.29, -24.1) * mm});
            skLineSegment(sketch, "E744", {"start": v(3.29, -24.1) * mm, "end": v(3.22, -24.48) * mm});
            skLineSegment(sketch, "E745", {"start": v(3.22, -24.48) * mm, "end": v(3.12, -24.9) * mm});
            skLineSegment(sketch, "E746", {"start": v(3.12, -24.9) * mm, "end": v(2.98, -25.38) * mm});
            skLineSegment(sketch, "E747", {"start": v(2.98, -25.38) * mm, "end": v(2.97, -25.43) * mm});
            skArc(sketch, "E748", {"start": v(2.97, -25.43) * mm, "mid": v(2.65, -25.46) * mm, "end": v(2.34, -25.5) * mm});
            skLineSegment(sketch, "E749", {"start": v(2.34, -25.5) * mm, "end": v(2.31, -25.45) * mm});
            skLineSegment(sketch, "E750", {"start": v(2.31, -25.45) * mm, "end": v(2.08, -25.01) * mm});
            skLineSegment(sketch, "E751", {"start": v(2.08, -25.01) * mm, "end": v(1.9, -24.62) * mm});
            skLineSegment(sketch, "E752", {"start": v(1.9, -24.62) * mm, "end": v(1.75, -24.27) * mm});
            skLineSegment(sketch, "E753", {"start": v(1.75, -24.27) * mm, "end": v(1.64, -23.97) * mm});
            skLineSegment(sketch, "E754", {"start": v(1.64, -23.97) * mm, "end": v(1.6, -23.82) * mm});
            skArc(sketch, "E755", {"start": v(1.6, -23.82) * mm, "mid": v(1.27, -23.84) * mm, "end": v(0.93, -23.86) * mm});
            skLineSegment(sketch, "E756", {"start": v(0.93, -23.86) * mm, "end": v(0.9, -24) * mm});
            skLineSegment(sketch, "E757", {"start": v(0.9, -24) * mm, "end": v(0.83, -24.32) * mm});
            skLineSegment(sketch, "E758", {"start": v(0.83, -24.32) * mm, "end": v(0.73, -24.68) * mm});
            skLineSegment(sketch, "E759", {"start": v(0.73, -24.68) * mm, "end": v(0.58, -25.1) * mm});
            skLineSegment(sketch, "E760", {"start": v(0.58, -25.1) * mm, "end": v(0.4, -25.55) * mm});
            skLineSegment(sketch, "E761", {"start": v(0.4, -25.55) * mm, "end": v(0.38, -25.6) * mm});
            skArc(sketch, "E762", {"start": v(0.38, -25.6) * mm, "mid": v(0.06, -25.6) * mm, "end": v(-0.25, -25.6) * mm});
            skLineSegment(sketch, "E763", {"start": v(-0.25, -25.6) * mm, "end": v(-0.28, -25.55) * mm});
            skLineSegment(sketch, "E764", {"start": v(-0.28, -25.55) * mm, "end": v(-0.46, -25.1) * mm});
            skLineSegment(sketch, "E765", {"start": v(-0.46, -25.1) * mm, "end": v(-0.6, -24.68) * mm});
            skLineSegment(sketch, "E766", {"start": v(-0.6, -24.68) * mm, "end": v(-0.71, -24.32) * mm});
            skLineSegment(sketch, "E767", {"start": v(-0.71, -24.32) * mm, "end": v(-0.8, -24) * mm});
            skLineSegment(sketch, "E768", {"start": v(-0.8, -24) * mm, "end": v(-0.82, -23.86) * mm});
            skArc(sketch, "E769", {"start": v(-0.82, -23.86) * mm, "mid": v(-1.15, -23.85) * mm, "end": v(-1.48, -23.83) * mm});
            skLineSegment(sketch, "E770", {"start": v(-1.48, -23.83) * mm, "end": v(-1.53, -23.97) * mm});
            skLineSegment(sketch, "E771", {"start": v(-1.53, -23.97) * mm, "end": v(-1.63, -24.28) * mm});
            skLineSegment(sketch, "E772", {"start": v(-1.63, -24.28) * mm, "end": v(-1.77, -24.63) * mm});
            skLineSegment(sketch, "E773", {"start": v(-1.77, -24.63) * mm, "end": v(-1.96, -25.02) * mm});
            skLineSegment(sketch, "E774", {"start": v(-1.96, -25.02) * mm, "end": v(-2.19, -25.46) * mm});
            skLineSegment(sketch, "E775", {"start": v(-2.19, -25.46) * mm, "end": v(-2.21, -25.5) * mm});
            skArc(sketch, "E776", {"start": v(-2.21, -25.5) * mm, "mid": v(-2.53, -25.47) * mm, "end": v(-2.84, -25.44) * mm});
            skLineSegment(sketch, "E777", {"start": v(-2.84, -25.44) * mm, "end": v(-2.86, -25.4) * mm});
            skLineSegment(sketch, "E778", {"start": v(-2.86, -25.4) * mm, "end": v(-3, -24.92) * mm});
            skLineSegment(sketch, "E779", {"start": v(-3, -24.92) * mm, "end": v(-3.1, -24.5) * mm});
            skLineSegment(sketch, "E780", {"start": v(-3.1, -24.5) * mm, "end": v(-3.17, -24.12) * mm});
            skLineSegment(sketch, "E781", {"start": v(-3.17, -24.12) * mm, "end": v(-3.22, -23.8) * mm});
            skLineSegment(sketch, "E782", {"start": v(-3.22, -23.8) * mm, "end": v(-3.23, -23.66) * mm});
            skArc(sketch, "E783", {"start": v(-3.23, -23.66) * mm, "mid": v(-3.56, -23.6) * mm, "end": v(-3.89, -23.56) * mm});
            skLineSegment(sketch, "E784", {"start": v(-3.89, -23.56) * mm, "end": v(-3.94, -23.7) * mm});
            skLineSegment(sketch, "E785", {"start": v(-3.94, -23.7) * mm, "end": v(-4.08, -23.99) * mm});
            skLineSegment(sketch, "E786", {"start": v(-4.08, -23.99) * mm, "end": v(-4.26, -24.32) * mm});
            skLineSegment(sketch, "E787", {"start": v(-4.26, -24.32) * mm, "end": v(-4.48, -24.7) * mm});
            skLineSegment(sketch, "E788", {"start": v(-4.48, -24.7) * mm, "end": v(-4.75, -25.1) * mm});
            skLineSegment(sketch, "E789", {"start": v(-4.75, -25.1) * mm, "end": v(-4.78, -25.15) * mm});
            skArc(sketch, "E790", {"start": v(-4.78, -25.15) * mm, "mid": v(-5.1, -25.09) * mm, "end": v(-5.4, -25.02) * mm});
            skLineSegment(sketch, "E791", {"start": v(-5.4, -25.02) * mm, "end": v(-5.41, -24.98) * mm});
            skLineSegment(sketch, "E792", {"start": v(-5.41, -24.98) * mm, "end": v(-5.5, -24.49) * mm});
            skLineSegment(sketch, "E793", {"start": v(-5.5, -24.49) * mm, "end": v(-5.56, -24.06) * mm});
            skLineSegment(sketch, "E794", {"start": v(-5.56, -24.06) * mm, "end": v(-5.6, -23.68) * mm});
            skLineSegment(sketch, "E795", {"start": v(-5.6, -23.68) * mm, "end": v(-5.6, -23.36) * mm});
            skLineSegment(sketch, "E796", {"start": v(-5.6, -23.36) * mm, "end": v(-5.6, -23.2) * mm});
            skArc(sketch, "E797", {"start": v(-5.6, -23.2) * mm, "mid": v(-5.93, -23.13) * mm, "end": v(-6.25, -23.04) * mm});
            skLineSegment(sketch, "E798", {"start": v(-6.25, -23.04) * mm, "end": v(-6.32, -23.17) * mm});
            skLineSegment(sketch, "E799", {"start": v(-6.32, -23.17) * mm, "end": v(-6.49, -23.45) * mm});
            skLineSegment(sketch, "E800", {"start": v(-6.49, -23.45) * mm, "end": v(-6.7, -23.77) * mm});
            skLineSegment(sketch, "E801", {"start": v(-6.7, -23.77) * mm, "end": v(-6.96, -24.12) * mm});
            skLineSegment(sketch, "E802", {"start": v(-6.96, -24.12) * mm, "end": v(-7.27, -24.5) * mm});
            skLineSegment(sketch, "E803", {"start": v(-7.27, -24.5) * mm, "end": v(-7.3, -24.54) * mm});
            skArc(sketch, "E804", {"start": v(-7.3, -24.54) * mm, "mid": v(-7.6, -24.44) * mm, "end": v(-7.9, -24.35) * mm});
            skLineSegment(sketch, "E805", {"start": v(-7.9, -24.35) * mm, "end": v(-7.91, -24.3) * mm});
            skLineSegment(sketch, "E806", {"start": v(-7.91, -24.3) * mm, "end": v(-7.95, -23.8) * mm});
            skLineSegment(sketch, "E807", {"start": v(-7.95, -23.8) * mm, "end": v(-7.97, -23.37) * mm});
            skLineSegment(sketch, "E808", {"start": v(-7.97, -23.37) * mm, "end": v(-7.96, -23) * mm});
            skLineSegment(sketch, "E809", {"start": v(-7.96, -23) * mm, "end": v(-7.94, -22.67) * mm});
            skLineSegment(sketch, "E810", {"start": v(-7.94, -22.67) * mm, "end": v(-7.92, -22.52) * mm});
            skArc(sketch, "E811", {"start": v(-7.92, -22.52) * mm, "mid": v(-8.24, -22.4) * mm, "end": v(-8.55, -22.3) * mm});
            skLineSegment(sketch, "E812", {"start": v(-8.55, -22.3) * mm, "end": v(-8.63, -22.42) * mm});
            skLineSegment(sketch, "E813", {"start": v(-8.63, -22.42) * mm, "end": v(-8.82, -22.67) * mm});
            skLineSegment(sketch, "E814", {"start": v(-8.82, -22.67) * mm, "end": v(-9.07, -22.97) * mm});
            skLineSegment(sketch, "E815", {"start": v(-9.07, -22.97) * mm, "end": v(-9.36, -23.29) * mm});
            skLineSegment(sketch, "E816", {"start": v(-9.36, -23.29) * mm, "end": v(-9.71, -23.64) * mm});
            skLineSegment(sketch, "E817", {"start": v(-9.71, -23.64) * mm, "end": v(-9.75, -23.67) * mm});
            skArc(sketch, "E818", {"start": v(-9.75, -23.67) * mm, "mid": v(-10.04, -23.55) * mm, "end": v(-10.33, -23.42) * mm});
            skLineSegment(sketch, "E819", {"start": v(-10.33, -23.42) * mm, "end": v(-10.33, -23.37) * mm});
            skLineSegment(sketch, "E820", {"start": v(-10.33, -23.37) * mm, "end": v(-10.32, -22.88) * mm});
            skLineSegment(sketch, "E821", {"start": v(-10.32, -22.88) * mm, "end": v(-10.3, -22.44) * mm});
            skLineSegment(sketch, "E822", {"start": v(-10.3, -22.44) * mm, "end": v(-10.25, -22.07) * mm});
            skLineSegment(sketch, "E823", {"start": v(-10.25, -22.07) * mm, "end": v(-10.2, -21.75) * mm});
            skLineSegment(sketch, "E824", {"start": v(-10.2, -21.75) * mm, "end": v(-10.16, -21.6) * mm});
            skArc(sketch, "E825", {"start": v(-10.16, -21.6) * mm, "mid": v(-10.46, -21.46) * mm, "end": v(-10.76, -21.31) * mm});
            skLineSegment(sketch, "E826", {"start": v(-10.76, -21.31) * mm, "end": v(-10.86, -21.43) * mm});
            skLineSegment(sketch, "E827", {"start": v(-10.86, -21.43) * mm, "end": v(-11.07, -21.66) * mm});
            skLineSegment(sketch, "E828", {"start": v(-11.07, -21.66) * mm, "end": v(-11.34, -21.93) * mm});
            skLineSegment(sketch, "E829", {"start": v(-11.34, -21.93) * mm, "end": v(-11.67, -22.22) * mm});
            skLineSegment(sketch, "E830", {"start": v(-11.67, -22.22) * mm, "end": v(-12.05, -22.53) * mm});
            skLineSegment(sketch, "E831", {"start": v(-12.05, -22.53) * mm, "end": v(-12.1, -22.56) * mm});
            skArc(sketch, "E832", {"start": v(-12.1, -22.56) * mm, "mid": v(-12.37, -22.41) * mm, "end": v(-12.65, -22.26) * mm});
            skLineSegment(sketch, "E833", {"start": v(-12.65, -22.26) * mm, "end": v(-12.64, -22.2) * mm});
            skLineSegment(sketch, "E834", {"start": v(-12.64, -22.2) * mm, "end": v(-12.58, -21.72) * mm});
            skLineSegment(sketch, "E835", {"start": v(-12.58, -21.72) * mm, "end": v(-12.5, -21.29) * mm});
            skLineSegment(sketch, "E836", {"start": v(-12.5, -21.29) * mm, "end": v(-12.43, -20.92) * mm});
            skLineSegment(sketch, "E837", {"start": v(-12.43, -20.92) * mm, "end": v(-12.34, -20.6) * mm});
            skLineSegment(sketch, "E838", {"start": v(-12.34, -20.6) * mm, "end": v(-12.3, -20.47) * mm});
            skArc(sketch, "E839", {"start": v(-12.3, -20.47) * mm, "mid": v(-12.58, -20.3) * mm, "end": v(-12.86, -20.11) * mm});
            skLineSegment(sketch, "E840", {"start": v(-12.86, -20.11) * mm, "end": v(-12.97, -20.22) * mm});
            skLineSegment(sketch, "E841", {"start": v(-12.97, -20.22) * mm, "end": v(-13.2, -20.43) * mm});
            skLineSegment(sketch, "E842", {"start": v(-13.2, -20.43) * mm, "end": v(-13.5, -20.67) * mm});
            skLineSegment(sketch, "E843", {"start": v(-13.5, -20.67) * mm, "end": v(-13.86, -20.93) * mm});
            skLineSegment(sketch, "E844", {"start": v(-13.86, -20.93) * mm, "end": v(-14.27, -21.2) * mm});
            skLineSegment(sketch, "E845", {"start": v(-14.27, -21.2) * mm, "end": v(-14.31, -21.23) * mm});
            skArc(sketch, "E846", {"start": v(-14.31, -21.23) * mm, "mid": v(-14.57, -21.05) * mm, "end": v(-14.83, -20.87) * mm});
            skLineSegment(sketch, "E847", {"start": v(-14.83, -20.87) * mm, "end": v(-14.82, -20.82) * mm});
            skLineSegment(sketch, "E848", {"start": v(-14.82, -20.82) * mm, "end": v(-14.72, -20.33) * mm});
            skLineSegment(sketch, "E849", {"start": v(-14.72, -20.33) * mm, "end": v(-14.6, -19.91) * mm});
            skLineSegment(sketch, "E850", {"start": v(-14.6, -19.91) * mm, "end": v(-14.48, -19.55) * mm});
            skLineSegment(sketch, "E851", {"start": v(-14.48, -19.55) * mm, "end": v(-14.36, -19.25) * mm});
            skLineSegment(sketch, "E852", {"start": v(-14.36, -19.25) * mm, "end": v(-14.3, -19.12) * mm});
            skArc(sketch, "E853", {"start": v(-14.3, -19.12) * mm, "mid": v(-14.57, -18.91) * mm, "end": v(-14.83, -18.7) * mm});
            skLineSegment(sketch, "E854", {"start": v(-14.83, -18.7) * mm, "end": v(-14.95, -18.8) * mm});
            skLineSegment(sketch, "E855", {"start": v(-14.95, -18.8) * mm, "end": v(-15.2, -19) * mm});
            skLineSegment(sketch, "E856", {"start": v(-15.2, -19) * mm, "end": v(-15.52, -19.2) * mm});
            skLineSegment(sketch, "E857", {"start": v(-15.52, -19.2) * mm, "end": v(-15.9, -19.42) * mm});
            skLineSegment(sketch, "E858", {"start": v(-15.9, -19.42) * mm, "end": v(-16.34, -19.65) * mm});
            skLineSegment(sketch, "E859", {"start": v(-16.34, -19.65) * mm, "end": v(-16.39, -19.67) * mm});
            skArc(sketch, "E860", {"start": v(-16.39, -19.67) * mm, "mid": v(-16.63, -19.46) * mm, "end": v(-16.87, -19.26) * mm});
            skLineSegment(sketch, "E861", {"start": v(-16.87, -19.26) * mm, "end": v(-16.85, -19.2) * mm});
            skLineSegment(sketch, "E862", {"start": v(-16.85, -19.2) * mm, "end": v(-16.7, -18.74) * mm});
            skLineSegment(sketch, "E863", {"start": v(-16.7, -18.74) * mm, "end": v(-16.54, -18.33) * mm});
            skLineSegment(sketch, "E864", {"start": v(-16.54, -18.33) * mm, "end": v(-16.38, -17.99) * mm});
            skLineSegment(sketch, "E865", {"start": v(-16.38, -17.99) * mm, "end": v(-16.24, -17.7) * mm});
            skLineSegment(sketch, "E866", {"start": v(-16.24, -17.7) * mm, "end": v(-16.16, -17.57) * mm});
            skArc(sketch, "E867", {"start": v(-16.16, -17.57) * mm, "mid": v(-16.4, -17.34) * mm, "end": v(-16.65, -17.11) * mm});
            skLineSegment(sketch, "E868", {"start": v(-16.65, -17.11) * mm, "end": v(-16.77, -17.2) * mm});
            skLineSegment(sketch, "E869", {"start": v(-16.77, -17.2) * mm, "end": v(-17.05, -17.36) * mm});
            skLineSegment(sketch, "E870", {"start": v(-17.05, -17.36) * mm, "end": v(-17.39, -17.53) * mm});
            skLineSegment(sketch, "E871", {"start": v(-17.39, -17.53) * mm, "end": v(-17.79, -17.71) * mm});
            skLineSegment(sketch, "E872", {"start": v(-17.79, -17.71) * mm, "end": v(-18.25, -17.9) * mm});
            skLineSegment(sketch, "E873", {"start": v(-18.25, -17.9) * mm, "end": v(-18.3, -17.9) * mm});
            skArc(sketch, "E874", {"start": v(-18.3, -17.9) * mm, "mid": v(-18.51, -17.68) * mm, "end": v(-18.73, -17.45) * mm});
            skLineSegment(sketch, "E875", {"start": v(-18.73, -17.45) * mm, "end": v(-18.71, -17.4) * mm});
            skLineSegment(sketch, "E876", {"start": v(-18.71, -17.4) * mm, "end": v(-18.5, -16.95) * mm});
            skLineSegment(sketch, "E877", {"start": v(-18.5, -16.95) * mm, "end": v(-18.3, -16.57) * mm});
            skLineSegment(sketch, "E878", {"start": v(-18.3, -16.57) * mm, "end": v(-18.12, -16.24) * mm});
            skLineSegment(sketch, "E879", {"start": v(-18.12, -16.24) * mm, "end": v(-17.95, -15.97) * mm});
            skLineSegment(sketch, "E880", {"start": v(-17.95, -15.97) * mm, "end": v(-17.86, -15.85) * mm});
            skArc(sketch, "E881", {"start": v(-17.86, -15.85) * mm, "mid": v(-18.08, -15.6) * mm, "end": v(-18.3, -15.34) * mm});
            skLineSegment(sketch, "E882", {"start": v(-18.3, -15.34) * mm, "end": v(-18.43, -15.4) * mm});
            skLineSegment(sketch, "E883", {"start": v(-18.43, -15.4) * mm, "end": v(-18.72, -15.54) * mm});
            skLineSegment(sketch, "E884", {"start": v(-18.72, -15.54) * mm, "end": v(-19.07, -15.68) * mm});
            skLineSegment(sketch, "E885", {"start": v(-19.07, -15.68) * mm, "end": v(-19.49, -15.82) * mm});
            skLineSegment(sketch, "E886", {"start": v(-19.49, -15.82) * mm, "end": v(-19.96, -15.96) * mm});
            skLineSegment(sketch, "E887", {"start": v(-19.96, -15.96) * mm, "end": v(-20.01, -15.97) * mm});
            skArc(sketch, "E888", {"start": v(-20.01, -15.97) * mm, "mid": v(-20.2, -15.72) * mm, "end": v(-20.4, -15.47) * mm});
            skLineSegment(sketch, "E889", {"start": v(-20.4, -15.47) * mm, "end": v(-20.38, -15.42) * mm});
            skLineSegment(sketch, "E890", {"start": v(-20.38, -15.42) * mm, "end": v(-20.13, -15) * mm});
            skLineSegment(sketch, "E891", {"start": v(-20.13, -15) * mm, "end": v(-19.9, -14.63) * mm});
            skLineSegment(sketch, "E892", {"start": v(-19.9, -14.63) * mm, "end": v(-19.67, -14.32) * mm});
            skLineSegment(sketch, "E893", {"start": v(-19.67, -14.32) * mm, "end": v(-19.47, -14.07) * mm});
            skLineSegment(sketch, "E894", {"start": v(-19.47, -14.07) * mm, "end": v(-19.37, -13.96) * mm});
            skArc(sketch, "E895", {"start": v(-19.37, -13.96) * mm, "mid": v(-19.56, -13.69) * mm, "end": v(-19.75, -13.41) * mm});
            skLineSegment(sketch, "E896", {"start": v(-19.75, -13.41) * mm, "end": v(-19.9, -13.47) * mm});
            skLineSegment(sketch, "E897", {"start": v(-19.9, -13.47) * mm, "end": v(-20.2, -13.57) * mm});
            skLineSegment(sketch, "E898", {"start": v(-20.2, -13.57) * mm, "end": v(-20.56, -13.67) * mm});
            skLineSegment(sketch, "E899", {"start": v(-20.56, -13.67) * mm, "end": v(-20.99, -13.77) * mm});
            skLineSegment(sketch, "E900", {"start": v(-20.99, -13.77) * mm, "end": v(-21.47, -13.85) * mm});
            skLineSegment(sketch, "E901", {"start": v(-21.47, -13.85) * mm, "end": v(-21.52, -13.86) * mm});
            skArc(sketch, "E902", {"start": v(-21.52, -13.86) * mm, "mid": v(-21.7, -13.6) * mm, "end": v(-21.86, -13.32) * mm});
            skLineSegment(sketch, "E903", {"start": v(-21.86, -13.32) * mm, "end": v(-21.83, -13.28) * mm});
            skLineSegment(sketch, "E904", {"start": v(-21.83, -13.28) * mm, "end": v(-21.54, -12.88) * mm});
            skLineSegment(sketch, "E905", {"start": v(-21.54, -12.88) * mm, "end": v(-21.27, -12.54) * mm});
            skLineSegment(sketch, "E906", {"start": v(-21.27, -12.54) * mm, "end": v(-21.02, -12.26) * mm});
            skLineSegment(sketch, "E907", {"start": v(-21.02, -12.26) * mm, "end": v(-20.8, -12.03) * mm});
            skLineSegment(sketch, "E908", {"start": v(-20.8, -12.03) * mm, "end": v(-20.68, -11.93) * mm});
            skArc(sketch, "E909", {"start": v(-20.68, -11.93) * mm, "mid": v(-20.85, -11.64) * mm, "end": v(-21, -11.34) * mm});
            skLineSegment(sketch, "E910", {"start": v(-21, -11.34) * mm, "end": v(-21.15, -11.38) * mm});
            skLineSegment(sketch, "E911", {"start": v(-21.15, -11.38) * mm, "end": v(-21.46, -11.46) * mm});
            skLineSegment(sketch, "E912", {"start": v(-21.46, -11.46) * mm, "end": v(-21.84, -11.52) * mm});
            skLineSegment(sketch, "E913", {"start": v(-21.84, -11.52) * mm, "end": v(-22.27, -11.57) * mm});
            skLineSegment(sketch, "E914", {"start": v(-22.27, -11.57) * mm, "end": v(-22.77, -11.61) * mm});
            skLineSegment(sketch, "E915", {"start": v(-22.77, -11.61) * mm, "end": v(-22.81, -11.61) * mm});
            skArc(sketch, "E916", {"start": v(-22.81, -11.61) * mm, "mid": v(-22.96, -11.33) * mm, "end": v(-23.1, -11.05) * mm});
            skLineSegment(sketch, "E917", {"start": v(-23.1, -11.05) * mm, "end": v(-23.06, -11) * mm});
            skLineSegment(sketch, "E918", {"start": v(-23.06, -11) * mm, "end": v(-22.73, -10.64) * mm});
            skLineSegment(sketch, "E919", {"start": v(-22.73, -10.64) * mm, "end": v(-22.43, -10.33) * mm});
            skLineSegment(sketch, "E920", {"start": v(-22.43, -10.33) * mm, "end": v(-22.15, -10.07) * mm});
            skLineSegment(sketch, "E921", {"start": v(-22.15, -10.07) * mm, "end": v(-21.9, -9.86) * mm});
            skLineSegment(sketch, "E922", {"start": v(-21.9, -9.86) * mm, "end": v(-21.78, -9.77) * mm});
            skArc(sketch, "E923", {"start": v(-21.78, -9.77) * mm, "mid": v(-21.92, -9.47) * mm, "end": v(-22.05, -9.16) * mm});
            skLineSegment(sketch, "E924", {"start": v(-22.05, -9.16) * mm, "end": v(-22.2, -9.19) * mm});
            skLineSegment(sketch, "E925", {"start": v(-22.2, -9.19) * mm, "end": v(-22.51, -9.23) * mm});
            skLineSegment(sketch, "E926", {"start": v(-22.51, -9.23) * mm, "end": v(-22.9, -9.25) * mm});
            skLineSegment(sketch, "E927", {"start": v(-22.9, -9.25) * mm, "end": v(-23.33, -9.26) * mm});
            skLineSegment(sketch, "E928", {"start": v(-23.33, -9.26) * mm, "end": v(-23.82, -9.25) * mm});
            skLineSegment(sketch, "E929", {"start": v(-23.82, -9.25) * mm, "end": v(-23.87, -9.24) * mm});
            skArc(sketch, "E930", {"start": v(-23.87, -9.24) * mm, "mid": v(-23.98, -8.95) * mm, "end": v(-24.1, -8.65) * mm});
            skLineSegment(sketch, "E931", {"start": v(-24.1, -8.65) * mm, "end": v(-24.06, -8.62) * mm});
            skLineSegment(sketch, "E932", {"start": v(-24.06, -8.62) * mm, "end": v(-23.7, -8.28) * mm});
            skLineSegment(sketch, "E933", {"start": v(-23.7, -8.28) * mm, "end": v(-23.36, -8) * mm});
            skLineSegment(sketch, "E934", {"start": v(-23.36, -8) * mm, "end": v(-23.05, -7.78) * mm});
            skLineSegment(sketch, "E935", {"start": v(-23.05, -7.78) * mm, "end": v(-22.79, -7.6) * mm});
            skLineSegment(sketch, "E936", {"start": v(-22.79, -7.6) * mm, "end": v(-22.66, -7.52) * mm});
            skArc(sketch, "E937", {"start": v(-22.66, -7.52) * mm, "mid": v(-22.76, -7.2) * mm, "end": v(-22.86, -6.88) * mm});
            skLineSegment(sketch, "E938", {"start": v(-22.86, -6.88) * mm, "end": v(-23.01, -6.9) * mm});
            skLineSegment(sketch, "E939", {"start": v(-23.01, -6.9) * mm, "end": v(-23.33, -6.9) * mm});
            skLineSegment(sketch, "E940", {"start": v(-23.33, -6.9) * mm, "end": v(-23.7, -6.89) * mm});
            skLineSegment(sketch, "E941", {"start": v(-23.7, -6.89) * mm, "end": v(-24.15, -6.85) * mm});
            skLineSegment(sketch, "E942", {"start": v(-24.15, -6.85) * mm, "end": v(-24.64, -6.8) * mm});
            skLineSegment(sketch, "E943", {"start": v(-24.64, -6.8) * mm, "end": v(-24.69, -6.78) * mm});
            skArc(sketch, "E944", {"start": v(-24.69, -6.78) * mm, "mid": v(-24.77, -6.48) * mm, "end": v(-24.85, -6.17) * mm});
            skLineSegment(sketch, "E945", {"start": v(-24.85, -6.17) * mm, "end": v(-24.8, -6.14) * mm});
            skLineSegment(sketch, "E946", {"start": v(-24.8, -6.14) * mm, "end": v(-24.41, -5.84) * mm});
            skLineSegment(sketch, "E947", {"start": v(-24.41, -5.84) * mm, "end": v(-24.05, -5.6) * mm});
            skLineSegment(sketch, "E948", {"start": v(-24.05, -5.6) * mm, "end": v(-23.72, -5.4) * mm});
            skLineSegment(sketch, "E949", {"start": v(-23.72, -5.4) * mm, "end": v(-23.44, -5.25) * mm});
            skLineSegment(sketch, "E950", {"start": v(-23.44, -5.25) * mm, "end": v(-23.3, -5.19) * mm});
            skArc(sketch, "E951", {"start": v(-23.3, -5.19) * mm, "mid": v(-23.37, -4.86) * mm, "end": v(-23.44, -4.54) * mm});
            skLineSegment(sketch, "E952", {"start": v(-23.44, -4.54) * mm, "end": v(-23.6, -4.53) * mm});
            skLineSegment(sketch, "E953", {"start": v(-23.6, -4.53) * mm, "end": v(-23.9, -4.5) * mm});
            skLineSegment(sketch, "E954", {"start": v(-23.9, -4.5) * mm, "end": v(-24.29, -4.46) * mm});
            skLineSegment(sketch, "E955", {"start": v(-24.29, -4.46) * mm, "end": v(-24.72, -4.38) * mm});
            skLineSegment(sketch, "E956", {"start": v(-24.72, -4.38) * mm, "end": v(-25.2, -4.26) * mm});
            skLineSegment(sketch, "E957", {"start": v(-25.2, -4.26) * mm, "end": v(-25.24, -4.25) * mm});
            skArc(sketch, "E958", {"start": v(-25.24, -4.25) * mm, "mid": v(-25.3, -3.94) * mm, "end": v(-25.34, -3.62) * mm});
            skLineSegment(sketch, "E959", {"start": v(-25.34, -3.62) * mm, "end": v(-25.3, -3.6) * mm});
            skLineSegment(sketch, "E960", {"start": v(-25.3, -3.6) * mm, "end": v(-24.88, -3.34) * mm});
            skLineSegment(sketch, "E961", {"start": v(-24.88, -3.34) * mm, "end": v(-24.5, -3.14) * mm});
            skLineSegment(sketch, "E962", {"start": v(-24.5, -3.14) * mm, "end": v(-24.15, -2.98) * mm});
            skLineSegment(sketch, "E963", {"start": v(-24.15, -2.98) * mm, "end": v(-23.85, -2.85) * mm});
            skLineSegment(sketch, "E964", {"start": v(-23.85, -2.85) * mm, "end": v(-23.7, -2.8) * mm});
            skArc(sketch, "E965", {"start": v(-23.7, -2.8) * mm, "mid": v(-23.75, -2.47) * mm, "end": v(-23.78, -2.14) * mm});
            skLineSegment(sketch, "E966", {"start": v(-23.78, -2.14) * mm, "end": v(-23.93, -2.12) * mm});
            skLineSegment(sketch, "E967", {"start": v(-23.93, -2.12) * mm, "end": v(-24.24, -2.06) * mm});
            skLineSegment(sketch, "E968", {"start": v(-24.24, -2.06) * mm, "end": v(-24.61, -1.98) * mm});
            skLineSegment(sketch, "E969", {"start": v(-24.61, -1.98) * mm, "end": v(-25.03, -1.85) * mm});
            skLineSegment(sketch, "E970", {"start": v(-25.03, -1.85) * mm, "end": v(-25.5, -1.7) * mm});
            skLineSegment(sketch, "E971", {"start": v(-25.5, -1.7) * mm, "end": v(-25.55, -1.67) * mm});
            skArc(sketch, "E972", {"start": v(-25.55, -1.67) * mm, "mid": v(-25.56, -1.36) * mm, "end": v(-25.58, -1.04) * mm});
            skLineSegment(sketch, "E973", {"start": v(-25.58, -1.04) * mm, "end": v(-25.53, -1.02) * mm});
            skLineSegment(sketch, "E974", {"start": v(-25.53, -1.02) * mm, "end": v(-25.09, -0.8) * mm});
            skLineSegment(sketch, "E975", {"start": v(-25.09, -0.8) * mm, "end": v(-24.68, -0.64) * mm});
            skLineSegment(sketch, "E976", {"start": v(-24.68, -0.64) * mm, "end": v(-24.32, -0.52) * mm});
            skLineSegment(sketch, "E977", {"start": v(-24.32, -0.52) * mm, "end": v(-24.02, -0.43) * mm});
            skLineSegment(sketch, "E978", {"start": v(-24.02, -0.43) * mm, "end": v(-23.87, -0.4) * mm});
            skArc(sketch, "E979", {"start": v(-23.87, -0.4) * mm, "mid": v(-23.87, -0.06) * mm, "end": v(-23.87, 0.28) * mm});
            skLineSegment(sketch, "E980", {"start": v(-23.87, 0.28) * mm, "end": v(-24.02, 0.31) * mm});
            skLineSegment(sketch, "E981", {"start": v(-24.02, 0.31) * mm, "end": v(-24.33, 0.4) * mm});
            skLineSegment(sketch, "E982", {"start": v(-24.33, 0.4) * mm, "end": v(-24.68, 0.52) * mm});
            skLineSegment(sketch, "E983", {"start": v(-24.68, 0.52) * mm, "end": v(-25.1, 0.69) * mm});
            skLineSegment(sketch, "E984", {"start": v(-25.1, 0.69) * mm, "end": v(-25.54, 0.9) * mm});
            skLineSegment(sketch, "E985", {"start": v(-25.54, 0.9) * mm, "end": v(-25.58, 0.92) * mm});
            skArc(sketch, "E986", {"start": v(-25.58, 0.92) * mm, "mid": v(-25.57, 1.24) * mm, "end": v(-25.55, 1.55) * mm});
            skLineSegment(sketch, "E987", {"start": v(-25.55, 1.55) * mm, "end": v(-25.5, 1.57) * mm});
            skLineSegment(sketch, "E988", {"start": v(-25.5, 1.57) * mm, "end": v(-25.04, 1.73) * mm});
            skLineSegment(sketch, "E989", {"start": v(-25.04, 1.73) * mm, "end": v(-24.62, 1.86) * mm});
            skLineSegment(sketch, "E990", {"start": v(-24.62, 1.86) * mm, "end": v(-24.25, 1.95) * mm});
            skLineSegment(sketch, "E991", {"start": v(-24.25, 1.95) * mm, "end": v(-23.94, 2) * mm});
            skLineSegment(sketch, "E992", {"start": v(-23.94, 2) * mm, "end": v(-23.79, 2.03) * mm});
            skArc(sketch, "E993", {"start": v(-23.79, 2.03) * mm, "mid": v(-23.76, 2.36) * mm, "end": v(-23.72, 2.69) * mm});
            skLineSegment(sketch, "E994", {"start": v(-23.72, 2.69) * mm, "end": v(-23.86, 2.74) * mm});
            skLineSegment(sketch, "E995", {"start": v(-23.86, 2.74) * mm, "end": v(-24.16, 2.86) * mm});
            skLineSegment(sketch, "E996", {"start": v(-24.16, 2.86) * mm, "end": v(-24.5, 3.02) * mm});
            skLineSegment(sketch, "E997", {"start": v(-24.5, 3.02) * mm, "end": v(-24.9, 3.22) * mm});
            skLineSegment(sketch, "E998", {"start": v(-24.9, 3.22) * mm, "end": v(-25.32, 3.48) * mm});
            skLineSegment(sketch, "E999", {"start": v(-25.32, 3.48) * mm, "end": v(-25.36, 3.5) * mm});
            skArc(sketch, "E1000", {"start": v(-25.36, 3.5) * mm, "mid": v(-25.31, 3.82) * mm, "end": v(-25.27, 4.13) * mm});
            skLineSegment(sketch, "E1001", {"start": v(-25.27, 4.13) * mm, "end": v(-25.22, 4.14) * mm});
            skLineSegment(sketch, "E1002", {"start": v(-25.22, 4.14) * mm, "end": v(-24.74, 4.26) * mm});
            skLineSegment(sketch, "E1003", {"start": v(-24.74, 4.26) * mm, "end": v(-24.3, 4.34) * mm});
            skLineSegment(sketch, "E1004", {"start": v(-24.3, 4.34) * mm, "end": v(-23.93, 4.39) * mm});
            skLineSegment(sketch, "E1005", {"start": v(-23.93, 4.39) * mm, "end": v(-23.61, 4.42) * mm});
            skLineSegment(sketch, "E1006", {"start": v(-23.61, 4.42) * mm, "end": v(-23.46, 4.42) * mm});
            skArc(sketch, "E1007", {"start": v(-23.46, 4.42) * mm, "mid": v(-23.4, 4.75) * mm, "end": v(-23.33, 5.08) * mm});
            skLineSegment(sketch, "E1008", {"start": v(-23.33, 5.08) * mm, "end": v(-23.47, 5.14) * mm});
            skLineSegment(sketch, "E1009", {"start": v(-23.47, 5.14) * mm, "end": v(-23.75, 5.29) * mm});
            skLineSegment(sketch, "E1010", {"start": v(-23.75, 5.29) * mm, "end": v(-24.07, 5.48) * mm});
            skLineSegment(sketch, "E1011", {"start": v(-24.07, 5.48) * mm, "end": v(-24.44, 5.72) * mm});
            skLineSegment(sketch, "E1012", {"start": v(-24.44, 5.72) * mm, "end": v(-24.84, 6.02) * mm});
            skLineSegment(sketch, "E1013", {"start": v(-24.84, 6.02) * mm, "end": v(-24.87, 6.05) * mm});
            skArc(sketch, "E1014", {"start": v(-24.87, 6.05) * mm, "mid": v(-24.8, 6.36) * mm, "end": v(-24.72, 6.66) * mm});
            skLineSegment(sketch, "E1015", {"start": v(-24.72, 6.66) * mm, "end": v(-24.67, 6.67) * mm});
            skLineSegment(sketch, "E1016", {"start": v(-24.67, 6.67) * mm, "end": v(-24.18, 6.74) * mm});
            skLineSegment(sketch, "E1017", {"start": v(-24.18, 6.74) * mm, "end": v(-23.74, 6.77) * mm});
            skLineSegment(sketch, "E1018", {"start": v(-23.74, 6.77) * mm, "end": v(-23.36, 6.79) * mm});
            skLineSegment(sketch, "E1019", {"start": v(-23.36, 6.79) * mm, "end": v(-23.04, 6.78) * mm});
            skLineSegment(sketch, "E1020", {"start": v(-23.04, 6.78) * mm, "end": v(-22.9, 6.77) * mm});
            skArc(sketch, "E1021", {"start": v(-22.9, 6.77) * mm, "mid": v(-22.8, 7.1) * mm, "end": v(-22.7, 7.41) * mm});
            skLineSegment(sketch, "E1022", {"start": v(-22.7, 7.41) * mm, "end": v(-22.82, 7.49) * mm});
            skLineSegment(sketch, "E1023", {"start": v(-22.82, 7.49) * mm, "end": v(-23.1, 7.67) * mm});
            skLineSegment(sketch, "E1024", {"start": v(-23.1, 7.67) * mm, "end": v(-23.4, 7.9) * mm});
            skLineSegment(sketch, "E1025", {"start": v(-23.4, 7.9) * mm, "end": v(-23.73, 8.17) * mm});
            skLineSegment(sketch, "E1026", {"start": v(-23.73, 8.17) * mm, "end": v(-24.1, 8.5) * mm});
            skLineSegment(sketch, "E1027", {"start": v(-24.1, 8.5) * mm, "end": v(-24.14, 8.54) * mm});
            skArc(sketch, "E1028", {"start": v(-24.14, 8.54) * mm, "mid": v(-24.03, 8.83) * mm, "end": v(-23.92, 9.13) * mm});
            skLineSegment(sketch, "E1029", {"start": v(-23.92, 9.13) * mm, "end": v(-23.87, 9.13) * mm});
            skLineSegment(sketch, "E1030", {"start": v(-23.87, 9.13) * mm, "end": v(-23.37, 9.15) * mm});
            skLineSegment(sketch, "E1031", {"start": v(-23.37, 9.15) * mm, "end": v(-22.94, 9.14) * mm});
            skLineSegment(sketch, "E1032", {"start": v(-22.94, 9.14) * mm, "end": v(-22.56, 9.12) * mm});
            skLineSegment(sketch, "E1033", {"start": v(-22.56, 9.12) * mm, "end": v(-22.24, 9.08) * mm});
            skLineSegment(sketch, "E1034", {"start": v(-22.24, 9.08) * mm, "end": v(-22.1, 9.05) * mm});
            skArc(sketch, "E1035", {"start": v(-22.1, 9.05) * mm, "mid": v(-21.96, 9.36) * mm, "end": v(-21.83, 9.67) * mm});
            skLineSegment(sketch, "E1036", {"start": v(-21.83, 9.67) * mm, "end": v(-21.95, 9.76) * mm});
            skLineSegment(sketch, "E1037", {"start": v(-21.95, 9.76) * mm, "end": v(-22.2, 9.96) * mm});
            skLineSegment(sketch, "E1038", {"start": v(-22.2, 9.96) * mm, "end": v(-22.48, 10.22) * mm});
            skLineSegment(sketch, "E1039", {"start": v(-22.48, 10.22) * mm, "end": v(-22.79, 10.53) * mm});
            skLineSegment(sketch, "E1040", {"start": v(-22.79, 10.53) * mm, "end": v(-23.12, 10.9) * mm});
            skLineSegment(sketch, "E1041", {"start": v(-23.12, 10.9) * mm, "end": v(-23.15, 10.93) * mm});
            skArc(sketch, "E1042", {"start": v(-23.15, 10.93) * mm, "mid": v(-23.01, 11.22) * mm, "end": v(-22.87, 11.5) * mm});
            skLineSegment(sketch, "E1043", {"start": v(-22.87, 11.5) * mm, "end": v(-22.82, 11.5) * mm});
            skLineSegment(sketch, "E1044", {"start": v(-22.82, 11.5) * mm, "end": v(-22.33, 11.47) * mm});
            skLineSegment(sketch, "E1045", {"start": v(-22.33, 11.47) * mm, "end": v(-21.9, 11.42) * mm});
            skLineSegment(sketch, "E1046", {"start": v(-21.9, 11.42) * mm, "end": v(-21.52, 11.35) * mm});
            skLineSegment(sketch, "E1047", {"start": v(-21.52, 11.35) * mm, "end": v(-21.2, 11.28) * mm});
            skLineSegment(sketch, "E1048", {"start": v(-21.2, 11.28) * mm, "end": v(-21.06, 11.24) * mm});
            skArc(sketch, "E1049", {"start": v(-21.06, 11.24) * mm, "mid": v(-20.9, 11.54) * mm, "end": v(-20.74, 11.83) * mm});
            skLineSegment(sketch, "E1050", {"start": v(-20.74, 11.83) * mm, "end": v(-20.85, 11.93) * mm});
            skLineSegment(sketch, "E1051", {"start": v(-20.85, 11.93) * mm, "end": v(-21.08, 12.16) * mm});
            skLineSegment(sketch, "E1052", {"start": v(-21.08, 12.16) * mm, "end": v(-21.33, 12.44) * mm});
            skLineSegment(sketch, "E1053", {"start": v(-21.33, 12.44) * mm, "end": v(-21.6, 12.78) * mm});
            skLineSegment(sketch, "E1054", {"start": v(-21.6, 12.78) * mm, "end": v(-21.9, 13.18) * mm});
            skLineSegment(sketch, "E1055", {"start": v(-21.9, 13.18) * mm, "end": v(-21.92, 13.22) * mm});
            skArc(sketch, "E1056", {"start": v(-21.92, 13.22) * mm, "mid": v(-21.76, 13.49) * mm, "end": v(-21.59, 13.76) * mm});
            skLineSegment(sketch, "E1057", {"start": v(-21.59, 13.76) * mm, "end": v(-21.54, 13.75) * mm});
            skLineSegment(sketch, "E1058", {"start": v(-21.54, 13.75) * mm, "end": v(-21.05, 13.67) * mm});
            skLineSegment(sketch, "E1059", {"start": v(-21.05, 13.67) * mm, "end": v(-20.63, 13.57) * mm});
            skLineSegment(sketch, "E1060", {"start": v(-20.63, 13.57) * mm, "end": v(-20.26, 13.47) * mm});
            skLineSegment(sketch, "E1061", {"start": v(-20.26, 13.47) * mm, "end": v(-19.96, 13.37) * mm});
            skLineSegment(sketch, "E1062", {"start": v(-19.96, 13.37) * mm, "end": v(-19.82, 13.32) * mm});
            skArc(sketch, "E1063", {"start": v(-19.82, 13.32) * mm, "mid": v(-19.63, 13.6) * mm, "end": v(-19.44, 13.86) * mm});
            skLineSegment(sketch, "E1064", {"start": v(-19.44, 13.86) * mm, "end": v(-19.54, 13.98) * mm});
            skLineSegment(sketch, "E1065", {"start": v(-19.54, 13.98) * mm, "end": v(-19.74, 14.23) * mm});
            skLineSegment(sketch, "E1066", {"start": v(-19.74, 14.23) * mm, "end": v(-19.96, 14.53) * mm});
            skLineSegment(sketch, "E1067", {"start": v(-19.96, 14.53) * mm, "end": v(-20.2, 14.9) * mm});
            skLineSegment(sketch, "E1068", {"start": v(-20.2, 14.9) * mm, "end": v(-20.45, 15.33) * mm});
            skLineSegment(sketch, "E1069", {"start": v(-20.45, 15.33) * mm, "end": v(-20.47, 15.37) * mm});
            skArc(sketch, "E1070", {"start": v(-20.47, 15.37) * mm, "mid": v(-20.28, 15.62) * mm, "end": v(-20.09, 15.87) * mm});
            skLineSegment(sketch, "E1071", {"start": v(-20.09, 15.87) * mm, "end": v(-20.04, 15.86) * mm});
            skLineSegment(sketch, "E1072", {"start": v(-20.04, 15.86) * mm, "end": v(-19.56, 15.73) * mm});
            skLineSegment(sketch, "E1073", {"start": v(-19.56, 15.73) * mm, "end": v(-19.15, 15.59) * mm});
            skLineSegment(sketch, "E1074", {"start": v(-19.15, 15.59) * mm, "end": v(-18.8, 15.45) * mm});
            skLineSegment(sketch, "E1075", {"start": v(-18.8, 15.45) * mm, "end": v(-18.5, 15.32) * mm});
            skLineSegment(sketch, "E1076", {"start": v(-18.5, 15.32) * mm, "end": v(-18.37, 15.25) * mm});
            skArc(sketch, "E1077", {"start": v(-18.37, 15.25) * mm, "mid": v(-18.15, 15.5) * mm, "end": v(-17.93, 15.76) * mm});
            skLineSegment(sketch, "E1078", {"start": v(-17.93, 15.76) * mm, "end": v(-18.02, 15.88) * mm});
            skLineSegment(sketch, "E1079", {"start": v(-18.02, 15.88) * mm, "end": v(-18.2, 16.15) * mm});
            skLineSegment(sketch, "E1080", {"start": v(-18.2, 16.15) * mm, "end": v(-18.39, 16.48) * mm});
            skLineSegment(sketch, "E1081", {"start": v(-18.39, 16.48) * mm, "end": v(-18.59, 16.87) * mm});
            skLineSegment(sketch, "E1082", {"start": v(-18.59, 16.87) * mm, "end": v(-18.8, 17.32) * mm});
            skLineSegment(sketch, "E1083", {"start": v(-18.8, 17.32) * mm, "end": v(-18.81, 17.36) * mm});
            skArc(sketch, "E1084", {"start": v(-18.81, 17.36) * mm, "mid": v(-18.6, 17.6) * mm, "end": v(-18.38, 17.82) * mm});
            skLineSegment(sketch, "E1085", {"start": v(-18.38, 17.82) * mm, "end": v(-18.33, 17.8) * mm});
            skLineSegment(sketch, "E1086", {"start": v(-18.33, 17.8) * mm, "end": v(-17.87, 17.63) * mm});
            skLineSegment(sketch, "E1087", {"start": v(-17.87, 17.63) * mm, "end": v(-17.47, 17.45) * mm});
            skLineSegment(sketch, "E1088", {"start": v(-17.47, 17.45) * mm, "end": v(-17.13, 17.27) * mm});
            skLineSegment(sketch, "E1089", {"start": v(-17.13, 17.27) * mm, "end": v(-16.86, 17.11) * mm});
            skLineSegment(sketch, "E1090", {"start": v(-16.86, 17.11) * mm, "end": v(-16.73, 17.03) * mm});
            skArc(sketch, "E1091", {"start": v(-16.73, 17.03) * mm, "mid": v(-16.5, 17.26) * mm, "end": v(-16.25, 17.5) * mm});
            skLineSegment(sketch, "E1092", {"start": v(-16.25, 17.5) * mm, "end": v(-16.32, 17.62) * mm});
            skLineSegment(sketch, "E1093", {"start": v(-16.32, 17.62) * mm, "end": v(-16.47, 17.9) * mm});
            skLineSegment(sketch, "E1094", {"start": v(-16.47, 17.9) * mm, "end": v(-16.63, 18.25) * mm});
            skLineSegment(sketch, "E1095", {"start": v(-16.63, 18.25) * mm, "end": v(-16.79, 18.66) * mm});
            skLineSegment(sketch, "E1096", {"start": v(-16.79, 18.66) * mm, "end": v(-16.95, 19.13) * mm});
            skLineSegment(sketch, "E1097", {"start": v(-16.95, 19.13) * mm, "end": v(-16.96, 19.18) * mm});
            skArc(sketch, "E1098", {"start": v(-16.96, 19.18) * mm, "mid": v(-16.72, 19.38) * mm, "end": v(-16.48, 19.59) * mm});
            skLineSegment(sketch, "E1099", {"start": v(-16.48, 19.59) * mm, "end": v(-16.44, 19.57) * mm});
            skLineSegment(sketch, "E1100", {"start": v(-16.44, 19.57) * mm, "end": v(-16, 19.34) * mm});
            skLineSegment(sketch, "E1101", {"start": v(-16, 19.34) * mm, "end": v(-15.62, 19.12) * mm});
            skLineSegment(sketch, "E1102", {"start": v(-15.62, 19.12) * mm, "end": v(-15.3, 18.92) * mm});
            skLineSegment(sketch, "E1103", {"start": v(-15.3, 18.92) * mm, "end": v(-15.04, 18.73) * mm});
            skLineSegment(sketch, "E1104", {"start": v(-15.04, 18.73) * mm, "end": v(-14.92, 18.64) * mm});
            skArc(sketch, "E1105", {"start": v(-14.92, 18.64) * mm, "mid": v(-14.66, 18.84) * mm, "end": v(-14.4, 19.05) * mm});
            skLineSegment(sketch, "E1106", {"start": v(-14.4, 19.05) * mm, "end": v(-14.46, 19.18) * mm});
            skLineSegment(sketch, "E1107", {"start": v(-14.46, 19.18) * mm, "end": v(-14.57, 19.48) * mm});
            skLineSegment(sketch, "E1108", {"start": v(-14.57, 19.48) * mm, "end": v(-14.7, 19.84) * mm});
            skLineSegment(sketch, "E1109", {"start": v(-14.7, 19.84) * mm, "end": v(-14.81, 20.26) * mm});
            skLineSegment(sketch, "E1110", {"start": v(-14.81, 20.26) * mm, "end": v(-14.92, 20.74) * mm});
            skLineSegment(sketch, "E1111", {"start": v(-14.92, 20.74) * mm, "end": v(-14.93, 20.8) * mm});
            skArc(sketch, "E1112", {"start": v(-14.93, 20.8) * mm, "mid": v(-14.68, 20.98) * mm, "end": v(-14.41, 21.16) * mm});
            skLineSegment(sketch, "E1113", {"start": v(-14.41, 21.16) * mm, "end": v(-14.37, 21.13) * mm});
            skLineSegment(sketch, "E1114", {"start": v(-14.37, 21.13) * mm, "end": v(-13.96, 20.86) * mm});
            skLineSegment(sketch, "E1115", {"start": v(-13.96, 20.86) * mm, "end": v(-13.6, 20.6) * mm});
            skLineSegment(sketch, "E1116", {"start": v(-13.6, 20.6) * mm, "end": v(-13.3, 20.37) * mm});
            skLineSegment(sketch, "E1117", {"start": v(-13.3, 20.37) * mm, "end": v(-13.07, 20.16) * mm});
            skLineSegment(sketch, "E1118", {"start": v(-13.07, 20.16) * mm, "end": v(-12.96, 20.05) * mm});
            skArc(sketch, "E1119", {"start": v(-12.96, 20.05) * mm, "mid": v(-12.68, 20.23) * mm, "end": v(-12.4, 20.4) * mm});
            skLineSegment(sketch, "E1120", {"start": v(-12.4, 20.4) * mm, "end": v(-12.44, 20.55) * mm});
            skLineSegment(sketch, "E1121", {"start": v(-12.44, 20.55) * mm, "end": v(-12.53, 20.86) * mm});
            skLineSegment(sketch, "E1122", {"start": v(-12.53, 20.86) * mm, "end": v(-12.61, 21.23) * mm});
            skLineSegment(sketch, "E1123", {"start": v(-12.61, 21.23) * mm, "end": v(-12.69, 21.66) * mm});
            skLineSegment(sketch, "E1124", {"start": v(-12.69, 21.66) * mm, "end": v(-12.75, 22.15) * mm});
            skLineSegment(sketch, "E1125", {"start": v(-12.75, 22.15) * mm, "end": v(-12.75, 22.2) * mm});
            skArc(sketch, "E1126", {"start": v(-12.75, 22.2) * mm, "mid": v(-12.48, 22.35) * mm, "end": v(-12.2, 22.5) * mm});
            skLineSegment(sketch, "E1127", {"start": v(-12.2, 22.5) * mm, "end": v(-12.16, 22.48) * mm});
            skLineSegment(sketch, "E1128", {"start": v(-12.16, 22.48) * mm, "end": v(-11.77, 22.17) * mm});
            skLineSegment(sketch, "E1129", {"start": v(-11.77, 22.17) * mm, "end": v(-11.45, 21.88) * mm});
            skLineSegment(sketch, "E1130", {"start": v(-11.45, 21.88) * mm, "end": v(-11.18, 21.61) * mm});
            skLineSegment(sketch, "E1131", {"start": v(-11.18, 21.61) * mm, "end": v(-10.96, 21.38) * mm});
            skLineSegment(sketch, "E1132", {"start": v(-10.96, 21.38) * mm, "end": v(-10.86, 21.26) * mm});
            skArc(sketch, "E1133", {"start": v(-10.86, 21.26) * mm, "mid": v(-10.57, 21.4) * mm, "end": v(-10.27, 21.55) * mm});
            skLineSegment(sketch, "E1134", {"start": v(-10.27, 21.55) * mm, "end": v(-10.3, 21.7) * mm});
            skLineSegment(sketch, "E1135", {"start": v(-10.3, 21.7) * mm, "end": v(-10.35, 22.02) * mm});
            skLineSegment(sketch, "E1136", {"start": v(-10.35, 22.02) * mm, "end": v(-10.4, 22.4) * mm});
            skLineSegment(sketch, "E1137", {"start": v(-10.4, 22.4) * mm, "end": v(-10.43, 22.83) * mm});
            skLineSegment(sketch, "E1138", {"start": v(-10.43, 22.83) * mm, "end": v(-10.44, 23.32) * mm});
            skLineSegment(sketch, "E1139", {"start": v(-10.44, 23.32) * mm, "end": v(-10.44, 23.37) * mm});
            skArc(sketch, "E1140", {"start": v(-10.44, 23.37) * mm, "mid": v(-10.15, 23.5) * mm, "end": v(-9.86, 23.62) * mm});
            skLineSegment(sketch, "E1141", {"start": v(-9.86, 23.62) * mm, "end": v(-9.82, 23.6) * mm});
            skLineSegment(sketch, "E1142", {"start": v(-9.82, 23.6) * mm, "end": v(-9.47, 23.24) * mm});
            skLineSegment(sketch, "E1143", {"start": v(-9.47, 23.24) * mm, "end": v(-9.18, 22.92) * mm});
            skLineSegment(sketch, "E1144", {"start": v(-9.18, 22.92) * mm, "end": v(-8.93, 22.63) * mm});
            skLineSegment(sketch, "E1145", {"start": v(-8.93, 22.63) * mm, "end": v(-8.74, 22.37) * mm});
            skLineSegment(sketch, "E1146", {"start": v(-8.74, 22.37) * mm, "end": v(-8.66, 22.25) * mm});
            skArc(sketch, "E1147", {"start": v(-8.66, 22.25) * mm, "mid": v(-8.35, 22.37) * mm, "end": v(-8.03, 22.48) * mm});
            skLineSegment(sketch, "E1148", {"start": v(-8.03, 22.48) * mm, "end": v(-8.05, 22.63) * mm});
            skLineSegment(sketch, "E1149", {"start": v(-8.05, 22.63) * mm, "end": v(-8.07, 22.95) * mm});
            skLineSegment(sketch, "E1150", {"start": v(-8.07, 22.95) * mm, "end": v(-8.08, 23.33) * mm});
            skLineSegment(sketch, "E1151", {"start": v(-8.08, 23.33) * mm, "end": v(-8.07, 23.77) * mm});
            skLineSegment(sketch, "E1152", {"start": v(-8.07, 23.77) * mm, "end": v(-8.03, 24.26) * mm});
            skLineSegment(sketch, "E1153", {"start": v(-8.03, 24.26) * mm, "end": v(-8.02, 24.31) * mm});
            skArc(sketch, "E1154", {"start": v(-8.02, 24.31) * mm, "mid": v(-7.72, 24.4) * mm, "end": v(-7.42, 24.5) * mm});
            skLineSegment(sketch, "E1155", {"start": v(-7.42, 24.5) * mm, "end": v(-7.39, 24.46) * mm});
            skLineSegment(sketch, "E1156", {"start": v(-7.39, 24.46) * mm, "end": v(-7.07, 24.08) * mm});
            skLineSegment(sketch, "E1157", {"start": v(-7.07, 24.08) * mm, "end": v(-6.8, 23.73) * mm});
            skLineSegment(sketch, "E1158", {"start": v(-6.8, 23.73) * mm, "end": v(-6.6, 23.42) * mm});
            skLineSegment(sketch, "E1159", {"start": v(-6.6, 23.42) * mm, "end": v(-6.43, 23.14) * mm});
            skLineSegment(sketch, "E1160", {"start": v(-6.43, 23.14) * mm, "end": v(-6.36, 23.01) * mm});
            skArc(sketch, "E1161", {"start": v(-6.36, 23.01) * mm, "mid": v(-6.04, 23.1) * mm, "end": v(-5.72, 23.18) * mm});
            skLineSegment(sketch, "E1162", {"start": v(-5.72, 23.18) * mm, "end": v(-5.72, 23.33) * mm});
            skLineSegment(sketch, "E1163", {"start": v(-5.72, 23.33) * mm, "end": v(-5.7, 23.65) * mm});
            skLineSegment(sketch, "E1164", {"start": v(-5.7, 23.65) * mm, "end": v(-5.68, 24.03) * mm});
            skLineSegment(sketch, "E1165", {"start": v(-5.68, 24.03) * mm, "end": v(-5.62, 24.46) * mm});
            skLineSegment(sketch, "E1166", {"start": v(-5.62, 24.46) * mm, "end": v(-5.53, 24.95) * mm});
            skLineSegment(sketch, "E1167", {"start": v(-5.53, 24.95) * mm, "end": v(-5.52, 25) * mm});
            skArc(sketch, "E1168", {"start": v(-5.52, 25) * mm, "mid": v(-5.21, 25.06) * mm, "end": v(-4.9, 25.13) * mm});
            skLineSegment(sketch, "E1169", {"start": v(-4.9, 25.13) * mm, "end": v(-4.87, 25.09) * mm});
            skLineSegment(sketch, "E1170", {"start": v(-4.87, 25.09) * mm, "end": v(-4.6, 24.67) * mm});
            skLineSegment(sketch, "E1171", {"start": v(-4.6, 24.67) * mm, "end": v(-4.37, 24.3) * mm});
            skLineSegment(sketch, "E1172", {"start": v(-4.37, 24.3) * mm, "end": v(-4.2, 23.97) * mm});
            skLineSegment(sketch, "E1173", {"start": v(-4.2, 23.97) * mm, "end": v(-4.06, 23.68) * mm});
            skLineSegment(sketch, "E1174", {"start": v(-4.06, 23.68) * mm, "end": v(-4, 23.54) * mm});
            skArc(sketch, "E1175", {"start": v(-4, 23.54) * mm, "mid": v(-3.67, 23.6) * mm, "end": v(-3.34, 23.64) * mm});
            skLineSegment(sketch, "E1176", {"start": v(-3.34, 23.64) * mm, "end": v(-3.33, 23.79) * mm});
            skLineSegment(sketch, "E1177", {"start": v(-3.33, 23.79) * mm, "end": v(-3.29, 24.1) * mm});
            skLineSegment(sketch, "E1178", {"start": v(-3.29, 24.1) * mm, "end": v(-3.22, 24.48) * mm});
            skLineSegment(sketch, "E1179", {"start": v(-3.22, 24.48) * mm, "end": v(-3.12, 24.9) * mm});
            skLineSegment(sketch, "E1180", {"start": v(-3.12, 24.9) * mm, "end": v(-2.98, 25.38) * mm});
            skLineSegment(sketch, "E1181", {"start": v(-2.98, 25.38) * mm, "end": v(-2.97, 25.43) * mm});
            skArc(sketch, "E1182", {"start": v(-2.97, 25.43) * mm, "mid": v(-2.65, 25.46) * mm, "end": v(-2.34, 25.5) * mm});
            skLineSegment(sketch, "E1183", {"start": v(-2.34, 25.5) * mm, "end": v(-2.31, 25.45) * mm});
            skLineSegment(sketch, "E1184", {"start": v(-2.31, 25.45) * mm, "end": v(-2.08, 25.01) * mm});
            skLineSegment(sketch, "E1185", {"start": v(-2.08, 25.01) * mm, "end": v(-1.9, 24.62) * mm});
            skLineSegment(sketch, "E1186", {"start": v(-1.9, 24.62) * mm, "end": v(-1.75, 24.27) * mm});
            skLineSegment(sketch, "E1187", {"start": v(-1.75, 24.27) * mm, "end": v(-1.64, 23.97) * mm});
            skLineSegment(sketch, "E1188", {"start": v(-1.64, 23.97) * mm, "end": v(-1.6, 23.82) * mm});
            skArc(sketch, "E1189", {"start": v(-1.6, 23.82) * mm, "mid": v(-1.27, 23.84) * mm, "end": v(-0.93, 23.86) * mm});
            skLineSegment(sketch, "E1190", {"start": v(-0.93, 23.86) * mm, "end": v(-0.9, 24) * mm});
            skLineSegment(sketch, "E1191", {"start": v(-0.9, 24) * mm, "end": v(-0.83, 24.32) * mm});
            skLineSegment(sketch, "E1192", {"start": v(-0.83, 24.32) * mm, "end": v(-0.73, 24.68) * mm});
            skLineSegment(sketch, "E1193", {"start": v(-0.73, 24.68) * mm, "end": v(-0.58, 25.1) * mm});
            skLineSegment(sketch, "E1194", {"start": v(-0.58, 25.1) * mm, "end": v(-0.4, 25.55) * mm});
            skLineSegment(sketch, "E1195", {"start": v(-0.4, 25.55) * mm, "end": v(-0.38, 25.6) * mm});
            skArc(sketch, "E1196", {"start": v(-0.38, 25.6) * mm, "mid": v(-0.06, 25.6) * mm, "end": v(0.25, 25.6) * mm});
            skLineSegment(sketch, "E1197", {"start": v(0.25, 25.6) * mm, "end": v(0.28, 25.55) * mm});
            skLineSegment(sketch, "E1198", {"start": v(0.28, 25.55) * mm, "end": v(0.46, 25.1) * mm});
            skLineSegment(sketch, "E1199", {"start": v(0.46, 25.1) * mm, "end": v(0.6, 24.68) * mm});
            skLineSegment(sketch, "E1200", {"start": v(0.6, 24.68) * mm, "end": v(0.71, 24.32) * mm});
            skLineSegment(sketch, "E1201", {"start": v(0.71, 24.32) * mm, "end": v(0.8, 24) * mm});
            skLineSegment(sketch, "E1202", {"start": v(0.8, 24) * mm, "end": v(0.82, 23.86) * mm});
            skArc(sketch, "E1203", {"start": v(0.82, 23.86) * mm, "mid": v(1.15, 23.85) * mm, "end": v(1.48, 23.83) * mm});
            skLineSegment(sketch, "E1204", {"start": v(1.48, 23.83) * mm, "end": v(1.53, 23.97) * mm});
            skLineSegment(sketch, "E1205", {"start": v(1.53, 23.97) * mm, "end": v(1.63, 24.28) * mm});
            skLineSegment(sketch, "E1206", {"start": v(1.63, 24.28) * mm, "end": v(1.77, 24.63) * mm});
            skLineSegment(sketch, "E1207", {"start": v(1.77, 24.63) * mm, "end": v(1.96, 25.02) * mm});
            skLineSegment(sketch, "E1208", {"start": v(1.96, 25.02) * mm, "end": v(2.19, 25.46) * mm});
            skLineSegment(sketch, "E1209", {"start": v(2.19, 25.46) * mm, "end": v(2.21, 25.5) * mm});
            skArc(sketch, "E1210", {"start": v(2.21, 25.5) * mm, "mid": v(2.53, 25.47) * mm, "end": v(2.84, 25.44) * mm});
            skLineSegment(sketch, "E1211", {"start": v(2.84, 25.44) * mm, "end": v(2.86, 25.4) * mm});
            skLineSegment(sketch, "E1212", {"start": v(2.86, 25.4) * mm, "end": v(3, 24.92) * mm});
            skLineSegment(sketch, "E1213", {"start": v(3, 24.92) * mm, "end": v(3.1, 24.5) * mm});
            skLineSegment(sketch, "E1214", {"start": v(3.1, 24.5) * mm, "end": v(3.17, 24.12) * mm});
            skLineSegment(sketch, "E1215", {"start": v(3.17, 24.12) * mm, "end": v(3.22, 23.8) * mm});
            skLineSegment(sketch, "E1216", {"start": v(3.22, 23.8) * mm, "end": v(3.23, 23.66) * mm});
            skArc(sketch, "E1217", {"start": v(3.23, 23.66) * mm, "mid": v(3.56, 23.6) * mm, "end": v(3.89, 23.56) * mm});
            skLineSegment(sketch, "E1218", {"start": v(3.89, 23.56) * mm, "end": v(3.94, 23.7) * mm});
            skLineSegment(sketch, "E1219", {"start": v(3.94, 23.7) * mm, "end": v(4.08, 23.99) * mm});
            skLineSegment(sketch, "E1220", {"start": v(4.08, 23.99) * mm, "end": v(4.26, 24.32) * mm});
            skLineSegment(sketch, "E1221", {"start": v(4.26, 24.32) * mm, "end": v(4.48, 24.7) * mm});
            skLineSegment(sketch, "E1222", {"start": v(4.48, 24.7) * mm, "end": v(4.75, 25.1) * mm});
            skLineSegment(sketch, "E1223", {"start": v(4.75, 25.1) * mm, "end": v(4.78, 25.15) * mm});
            skArc(sketch, "E1224", {"start": v(4.78, 25.15) * mm, "mid": v(5.1, 25.09) * mm, "end": v(5.4, 25.02) * mm});
            skLineSegment(sketch, "E1225", {"start": v(5.4, 25.02) * mm, "end": v(5.41, 24.98) * mm});
            skLineSegment(sketch, "E1226", {"start": v(5.41, 24.98) * mm, "end": v(5.5, 24.49) * mm});
            skLineSegment(sketch, "E1227", {"start": v(5.5, 24.49) * mm, "end": v(5.56, 24.06) * mm});
            skLineSegment(sketch, "E1228", {"start": v(5.56, 24.06) * mm, "end": v(5.6, 23.68) * mm});
            skLineSegment(sketch, "E1229", {"start": v(5.6, 23.68) * mm, "end": v(5.6, 23.36) * mm});
            skLineSegment(sketch, "E1230", {"start": v(5.6, 23.36) * mm, "end": v(5.6, 23.2) * mm});
            skArc(sketch, "E1231", {"start": v(5.6, 23.2) * mm, "mid": v(5.93, 23.13) * mm, "end": v(6.25, 23.04) * mm});
            skLineSegment(sketch, "E1232", {"start": v(6.25, 23.04) * mm, "end": v(6.32, 23.17) * mm});
            skLineSegment(sketch, "E1233", {"start": v(6.32, 23.17) * mm, "end": v(6.49, 23.45) * mm});
            skLineSegment(sketch, "E1234", {"start": v(6.49, 23.45) * mm, "end": v(6.7, 23.77) * mm});
            skLineSegment(sketch, "E1235", {"start": v(6.7, 23.77) * mm, "end": v(6.96, 24.12) * mm});
            skLineSegment(sketch, "E1236", {"start": v(6.96, 24.12) * mm, "end": v(7.27, 24.5) * mm});
            skLineSegment(sketch, "E1237", {"start": v(7.27, 24.5) * mm, "end": v(7.3, 24.54) * mm});
            skArc(sketch, "E1238", {"start": v(7.3, 24.54) * mm, "mid": v(7.6, 24.44) * mm, "end": v(7.9, 24.35) * mm});
            skLineSegment(sketch, "E1239", {"start": v(7.9, 24.35) * mm, "end": v(7.91, 24.3) * mm});
            skLineSegment(sketch, "E1240", {"start": v(7.91, 24.3) * mm, "end": v(7.95, 23.8) * mm});
            skLineSegment(sketch, "E1241", {"start": v(7.95, 23.8) * mm, "end": v(7.97, 23.37) * mm});
            skLineSegment(sketch, "E1242", {"start": v(7.97, 23.37) * mm, "end": v(7.96, 23) * mm});
            skLineSegment(sketch, "E1243", {"start": v(7.96, 23) * mm, "end": v(7.94, 22.67) * mm});
            skLineSegment(sketch, "E1244", {"start": v(7.94, 22.67) * mm, "end": v(7.92, 22.52) * mm});
            skArc(sketch, "E1245", {"start": v(7.92, 22.52) * mm, "mid": v(8.24, 22.4) * mm, "end": v(8.55, 22.3) * mm});
            skLineSegment(sketch, "E1246", {"start": v(8.55, 22.3) * mm, "end": v(8.63, 22.42) * mm});
            skLineSegment(sketch, "E1247", {"start": v(8.63, 22.42) * mm, "end": v(8.82, 22.67) * mm});
            skLineSegment(sketch, "E1248", {"start": v(8.82, 22.67) * mm, "end": v(9.07, 22.97) * mm});
            skLineSegment(sketch, "E1249", {"start": v(9.07, 22.97) * mm, "end": v(9.36, 23.29) * mm});
            skLineSegment(sketch, "E1250", {"start": v(9.36, 23.29) * mm, "end": v(9.71, 23.64) * mm});
            skLineSegment(sketch, "E1251", {"start": v(9.71, 23.64) * mm, "end": v(9.75, 23.67) * mm});
            skArc(sketch, "E1252", {"start": v(9.75, 23.67) * mm, "mid": v(10.04, 23.55) * mm, "end": v(10.33, 23.42) * mm});
            skLineSegment(sketch, "E1253", {"start": v(10.33, 23.42) * mm, "end": v(10.33, 23.37) * mm});
            skLineSegment(sketch, "E1254", {"start": v(10.33, 23.37) * mm, "end": v(10.32, 22.88) * mm});
            skLineSegment(sketch, "E1255", {"start": v(10.32, 22.88) * mm, "end": v(10.3, 22.44) * mm});
            skLineSegment(sketch, "E1256", {"start": v(10.3, 22.44) * mm, "end": v(10.25, 22.07) * mm});
            skLineSegment(sketch, "E1257", {"start": v(10.25, 22.07) * mm, "end": v(10.2, 21.75) * mm});
            skLineSegment(sketch, "E1258", {"start": v(10.2, 21.75) * mm, "end": v(10.16, 21.6) * mm});
            skArc(sketch, "E1259", {"start": v(10.16, 21.6) * mm, "mid": v(10.46, 21.46) * mm, "end": v(10.76, 21.31) * mm});
            skLineSegment(sketch, "E1260", {"start": v(10.76, 21.31) * mm, "end": v(10.86, 21.43) * mm});
            skLineSegment(sketch, "E1261", {"start": v(10.86, 21.43) * mm, "end": v(11.07, 21.66) * mm});
            skLineSegment(sketch, "E1262", {"start": v(11.07, 21.66) * mm, "end": v(11.34, 21.93) * mm});
            skLineSegment(sketch, "E1263", {"start": v(11.34, 21.93) * mm, "end": v(11.67, 22.22) * mm});
            skLineSegment(sketch, "E1264", {"start": v(11.67, 22.22) * mm, "end": v(12.05, 22.53) * mm});
            skLineSegment(sketch, "E1265", {"start": v(12.05, 22.53) * mm, "end": v(12.1, 22.56) * mm});
            skArc(sketch, "E1266", {"start": v(12.1, 22.56) * mm, "mid": v(12.37, 22.41) * mm, "end": v(12.65, 22.26) * mm});
            skLineSegment(sketch, "E1267", {"start": v(12.65, 22.26) * mm, "end": v(12.64, 22.2) * mm});
            skLineSegment(sketch, "E1268", {"start": v(12.64, 22.2) * mm, "end": v(12.58, 21.72) * mm});
            skLineSegment(sketch, "E1269", {"start": v(12.58, 21.72) * mm, "end": v(12.5, 21.29) * mm});
            skLineSegment(sketch, "E1270", {"start": v(12.5, 21.29) * mm, "end": v(12.43, 20.92) * mm});
            skLineSegment(sketch, "E1271", {"start": v(12.43, 20.92) * mm, "end": v(12.34, 20.6) * mm});
            skLineSegment(sketch, "E1272", {"start": v(12.34, 20.6) * mm, "end": v(12.3, 20.47) * mm});
            skArc(sketch, "E1273", {"start": v(12.3, 20.47) * mm, "mid": v(12.58, 20.3) * mm, "end": v(12.86, 20.11) * mm});
            skLineSegment(sketch, "E1274", {"start": v(12.86, 20.11) * mm, "end": v(12.97, 20.22) * mm});
            skLineSegment(sketch, "E1275", {"start": v(12.97, 20.22) * mm, "end": v(13.2, 20.43) * mm});
            skLineSegment(sketch, "E1276", {"start": v(13.2, 20.43) * mm, "end": v(13.5, 20.67) * mm});
            skLineSegment(sketch, "E1277", {"start": v(13.5, 20.67) * mm, "end": v(13.86, 20.93) * mm});
            skLineSegment(sketch, "E1278", {"start": v(13.86, 20.93) * mm, "end": v(14.27, 21.2) * mm});
            skLineSegment(sketch, "E1279", {"start": v(14.27, 21.2) * mm, "end": v(14.31, 21.23) * mm});
            skArc(sketch, "E1280", {"start": v(14.31, 21.23) * mm, "mid": v(14.57, 21.05) * mm, "end": v(14.83, 20.87) * mm});
            skLineSegment(sketch, "E1281", {"start": v(14.83, 20.87) * mm, "end": v(14.82, 20.82) * mm});
            skLineSegment(sketch, "E1282", {"start": v(14.82, 20.82) * mm, "end": v(14.72, 20.33) * mm});
            skLineSegment(sketch, "E1283", {"start": v(14.72, 20.33) * mm, "end": v(14.6, 19.91) * mm});
            skLineSegment(sketch, "E1284", {"start": v(14.6, 19.91) * mm, "end": v(14.48, 19.55) * mm});
            skLineSegment(sketch, "E1285", {"start": v(14.48, 19.55) * mm, "end": v(14.36, 19.25) * mm});
            skLineSegment(sketch, "E1286", {"start": v(14.36, 19.25) * mm, "end": v(14.3, 19.12) * mm});
            skArc(sketch, "E1287", {"start": v(14.3, 19.12) * mm, "mid": v(14.57, 18.91) * mm, "end": v(14.83, 18.7) * mm});
            skLineSegment(sketch, "E1288", {"start": v(14.83, 18.7) * mm, "end": v(14.95, 18.8) * mm});
            skLineSegment(sketch, "E1289", {"start": v(14.95, 18.8) * mm, "end": v(15.2, 19) * mm});
            skLineSegment(sketch, "E1290", {"start": v(15.2, 19) * mm, "end": v(15.52, 19.2) * mm});
            skLineSegment(sketch, "E1291", {"start": v(15.52, 19.2) * mm, "end": v(15.9, 19.42) * mm});
            skLineSegment(sketch, "E1292", {"start": v(15.9, 19.42) * mm, "end": v(16.34, 19.65) * mm});
            skLineSegment(sketch, "E1293", {"start": v(16.34, 19.65) * mm, "end": v(16.39, 19.67) * mm});
            skArc(sketch, "E1294", {"start": v(16.39, 19.67) * mm, "mid": v(16.63, 19.46) * mm, "end": v(16.87, 19.26) * mm});
            skLineSegment(sketch, "E1295", {"start": v(16.87, 19.26) * mm, "end": v(16.85, 19.2) * mm});
            skLineSegment(sketch, "E1296", {"start": v(16.85, 19.2) * mm, "end": v(16.7, 18.74) * mm});
            skLineSegment(sketch, "E1297", {"start": v(16.7, 18.74) * mm, "end": v(16.54, 18.33) * mm});
            skLineSegment(sketch, "E1298", {"start": v(16.54, 18.33) * mm, "end": v(16.38, 17.99) * mm});
            skLineSegment(sketch, "E1299", {"start": v(16.38, 17.99) * mm, "end": v(16.24, 17.7) * mm});
            skLineSegment(sketch, "E1300", {"start": v(16.24, 17.7) * mm, "end": v(16.16, 17.57) * mm});
            skArc(sketch, "E1301", {"start": v(16.16, 17.57) * mm, "mid": v(16.4, 17.34) * mm, "end": v(16.65, 17.11) * mm});
            skLineSegment(sketch, "E1302", {"start": v(16.65, 17.11) * mm, "end": v(16.77, 17.2) * mm});
            skLineSegment(sketch, "E1303", {"start": v(16.77, 17.2) * mm, "end": v(17.05, 17.36) * mm});
            skLineSegment(sketch, "E1304", {"start": v(17.05, 17.36) * mm, "end": v(17.39, 17.53) * mm});
            skLineSegment(sketch, "E1305", {"start": v(17.39, 17.53) * mm, "end": v(17.79, 17.71) * mm});
            skLineSegment(sketch, "E1306", {"start": v(17.79, 17.71) * mm, "end": v(18.25, 17.9) * mm});
            skLineSegment(sketch, "E1307", {"start": v(18.25, 17.9) * mm, "end": v(18.3, 17.9) * mm});
            skArc(sketch, "E1308", {"start": v(18.3, 17.9) * mm, "mid": v(18.51, 17.68) * mm, "end": v(18.73, 17.45) * mm});
            skLineSegment(sketch, "E1309", {"start": v(18.73, 17.45) * mm, "end": v(18.71, 17.4) * mm});
            skLineSegment(sketch, "E1310", {"start": v(18.71, 17.4) * mm, "end": v(18.5, 16.95) * mm});
            skLineSegment(sketch, "E1311", {"start": v(18.5, 16.95) * mm, "end": v(18.3, 16.57) * mm});
            skLineSegment(sketch, "E1312", {"start": v(18.3, 16.57) * mm, "end": v(18.12, 16.24) * mm});
            skLineSegment(sketch, "E1313", {"start": v(18.12, 16.24) * mm, "end": v(17.95, 15.97) * mm});
            skLineSegment(sketch, "E1314", {"start": v(17.95, 15.97) * mm, "end": v(17.86, 15.85) * mm});
            skArc(sketch, "E1315", {"start": v(17.86, 15.85) * mm, "mid": v(18.08, 15.6) * mm, "end": v(18.3, 15.34) * mm});
            skCircle(sketch, "E1316", {"center": v(0, 0) * mm, "radius": 2.5 * mm});
            skCircle(sketch, "E1317", {"center": v(-15, 0) * mm, "radius": 6 * mm});
            skCircle(sketch, "E1318", {"center": v(0, 15) * mm, "radius": 6 * mm});
            skCircle(sketch, "E1319", {"center": v(15, 0) * mm, "radius": 6 * mm});
            skCircle(sketch, "E1320", {"center": v(0, -15) * mm, "radius": 6 * mm});
            skCircle(sketch, "E1321", {"center": v(0, 0) * mm, "radius": 3.55 * mm});
            skSolve(sketch);
        }
        {
            assignVariable(context, id + "F1", {"name" : "Gear1width", "anyValue" : 6});
        }
        {
            assignVariable(context, id + "F2", {"name" : "Gear2width", "anyValue" : 12});
        }
        {
            var Q0;
            Q0=makeQuery(id+"F0.imprint","IMPRINT",FACE,{"disambiguationData":[TD([[makeQuery(id+"F0.imprint","IMPRINT",EDGE,{"derivedFrom":sQuery(id+"F0.wireOp",EDGE,"E0")}),-1.0]])]});
            extrude(context, id + "F3", {"entities" : qUnion([Q0]), "depth" : (getVariable(context, 'Gear2width')) * mm});
        }
        {
            var Q0;
            Q0 = qSketchRegion(id + "F0", true);
            extrude(context, id + "F4", {"entities" : qUnion([Q0]), "operationType" : NewBodyOperationType.ADD, "depth" : (getVariable(context, 'Gear1width')) * mm});
        }
        {
            var Q0;
            Q0=makeQuery(id+"F0.imprint","IMPRINT",FACE,{"disambiguationData":[TD([[makeQuery(id+"F0.imprint","IMPRINT",EDGE,{"derivedFrom":sQuery(id+"F0.wireOp",EDGE,"E1316")}),1.0]])]});
            extrude(context, id + "F5", {"entities" : qUnion([Q0]), "operationType" : NewBodyOperationType.ADD, "depth" : (getVariable(context, 'Gear2width') + 1) * mm, "hasSecondDirection" : true, "secondDirectionOppositeDirection" : true, "secondDirectionDepth" : 1 * mm});
        }
    });
